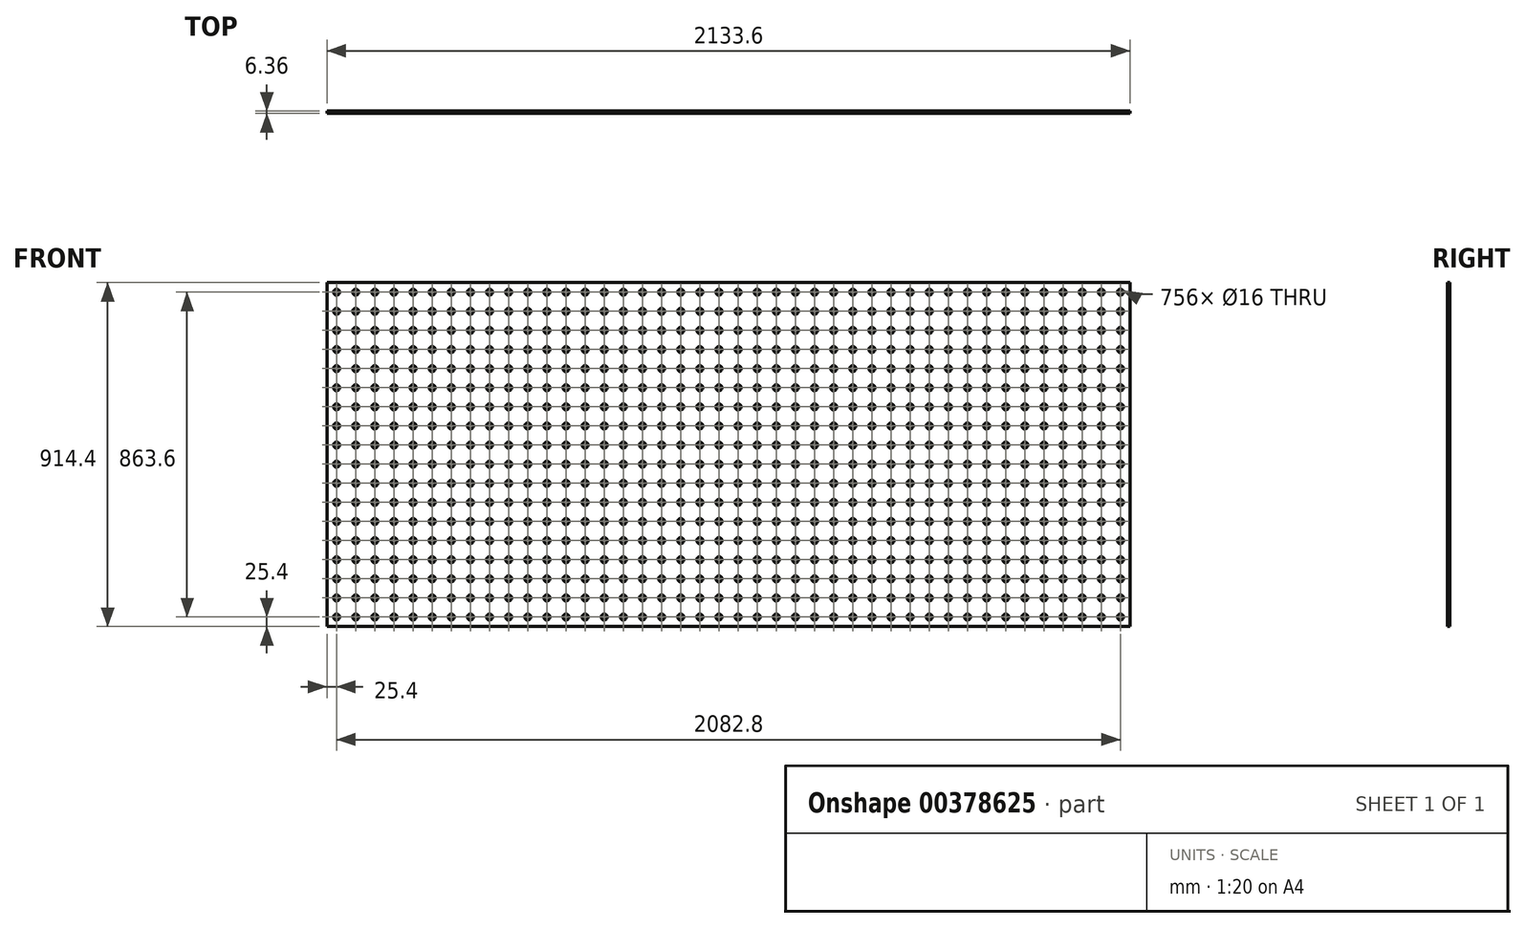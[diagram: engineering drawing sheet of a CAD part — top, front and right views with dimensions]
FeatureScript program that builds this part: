
annotation { "Feature Type Name" : "Feature", "Feature Type Description" : "" }
export const myFeature = defineFeature(function(context is Context, id is Id, definition is map)
    precondition{}
    {
        {
            var Q0;
            Q0=qCreatedBy(makeId("Front.planeOp"),FACE);
            var sketch = newSketch(context, id + "F0", { "sketchPlane" : qUnion([Q0])});
            skLineSegment(sketch, "E0.bottom", {"start": v(1066.8, 457.2) * mm, "end": v(-1066.8, 457.2) * mm});
            skLineSegment(sketch, "E0.top", {"start": v(1066.8, -457.2) * mm, "end": v(-1066.8, -457.2) * mm});
            skLineSegment(sketch, "E0.left", {"start": v(1066.8, 457.2) * mm, "end": v(1066.8, -457.2) * mm});
            skLineSegment(sketch, "E0.right", {"start": v(-1066.8, 457.2) * mm, "end": v(-1066.8, -457.2) * mm});
            skPoint(sketch, "E0.middle", {"position": v(0, 0) * mm});
            skSolve(sketch);
        }
        {
            var Q0;
            Q0 = qSketchRegion(id + "F0", true);
            extrude(context, id + "F1", {"entities" : qUnion([Q0]), "endBound" : BoundingType.SYMMETRIC, "depth" : 6.35 * mm});
        }
        {
            var Q0;
            Q0=makeQuery(id+"F1.opExtrude","CAP_FACE",FACE,{"disambiguationData":[OSD([sQuery(id+"F0.wireOp",EDGE,"E0.bottom"),sQuery(id+"F0.wireOp",EDGE,"E0.top"),sQuery(id+"F0.wireOp",EDGE,"E0.left"),sQuery(id+"F0.wireOp",EDGE,"E0.right")])],"isStart":false});
            var sketch = newSketch(context, id + "F2", { "sketchPlane" : qUnion([Q0])});
            skCircle(sketch, "E1", {"center": v(-1041.4, -431.8) * mm, "radius": 8 * mm});
            skCircle(sketch, "E2.0.1.0", {"center": v(-1041.4, -381) * mm, "radius": 8 * mm});
            skCircle(sketch, "E2.0.2.0", {"center": v(-1041.4, -330.2) * mm, "radius": 8 * mm});
            skCircle(sketch, "E2.0.3.0", {"center": v(-1041.4, -279.4) * mm, "radius": 8 * mm});
            skCircle(sketch, "E2.0.4.0", {"center": v(-1041.4, -228.6) * mm, "radius": 8 * mm});
            skCircle(sketch, "E2.0.5.0", {"center": v(-1041.4, -177.8) * mm, "radius": 8 * mm});
            skCircle(sketch, "E2.0.6.0", {"center": v(-1041.4, -127) * mm, "radius": 8 * mm});
            skCircle(sketch, "E2.0.7.0", {"center": v(-1041.4, -76.2) * mm, "radius": 8 * mm});
            skCircle(sketch, "E2.0.8.0", {"center": v(-1041.4, -25.4) * mm, "radius": 8 * mm});
            skCircle(sketch, "E2.0.9.0", {"center": v(-1041.4, 25.4) * mm, "radius": 8 * mm});
            skCircle(sketch, "E2.0.10.0", {"center": v(-1041.4, 76.2) * mm, "radius": 8 * mm});
            skCircle(sketch, "E2.0.11.0", {"center": v(-1041.4, 127) * mm, "radius": 8 * mm});
            skCircle(sketch, "E2.0.12.0", {"center": v(-1041.4, 177.8) * mm, "radius": 8 * mm});
            skCircle(sketch, "E2.0.13.0", {"center": v(-1041.4, 228.6) * mm, "radius": 8 * mm});
            skCircle(sketch, "E2.0.14.0", {"center": v(-1041.4, 279.4) * mm, "radius": 8 * mm});
            skCircle(sketch, "E2.0.15.0", {"center": v(-1041.4, 330.2) * mm, "radius": 8 * mm});
            skCircle(sketch, "E2.0.16.0", {"center": v(-1041.4, 381) * mm, "radius": 8 * mm});
            skCircle(sketch, "E2.0.17.0", {"center": v(-1041.4, 431.8) * mm, "radius": 8 * mm});
            skCircle(sketch, "E2.1.0.0", {"center": v(-990.6, -431.8) * mm, "radius": 8 * mm});
            skCircle(sketch, "E2.1.1.0", {"center": v(-990.6, -381) * mm, "radius": 8 * mm});
            skCircle(sketch, "E2.1.2.0", {"center": v(-990.6, -330.2) * mm, "radius": 8 * mm});
            skCircle(sketch, "E2.1.3.0", {"center": v(-990.6, -279.4) * mm, "radius": 8 * mm});
            skCircle(sketch, "E2.1.4.0", {"center": v(-990.6, -228.6) * mm, "radius": 8 * mm});
            skCircle(sketch, "E2.1.5.0", {"center": v(-990.6, -177.8) * mm, "radius": 8 * mm});
            skCircle(sketch, "E2.1.6.0", {"center": v(-990.6, -127) * mm, "radius": 8 * mm});
            skCircle(sketch, "E2.1.7.0", {"center": v(-990.6, -76.2) * mm, "radius": 8 * mm});
            skCircle(sketch, "E2.1.8.0", {"center": v(-990.6, -25.4) * mm, "radius": 8 * mm});
            skCircle(sketch, "E2.1.9.0", {"center": v(-990.6, 25.4) * mm, "radius": 8 * mm});
            skCircle(sketch, "E2.1.10.0", {"center": v(-990.6, 76.2) * mm, "radius": 8 * mm});
            skCircle(sketch, "E2.1.11.0", {"center": v(-990.6, 127) * mm, "radius": 8 * mm});
            skCircle(sketch, "E2.1.12.0", {"center": v(-990.6, 177.8) * mm, "radius": 8 * mm});
            skCircle(sketch, "E2.1.13.0", {"center": v(-990.6, 228.6) * mm, "radius": 8 * mm});
            skCircle(sketch, "E2.1.14.0", {"center": v(-990.6, 279.4) * mm, "radius": 8 * mm});
            skCircle(sketch, "E2.1.15.0", {"center": v(-990.6, 330.2) * mm, "radius": 8 * mm});
            skCircle(sketch, "E2.1.16.0", {"center": v(-990.6, 381) * mm, "radius": 8 * mm});
            skCircle(sketch, "E2.1.17.0", {"center": v(-990.6, 431.8) * mm, "radius": 8 * mm});
            skCircle(sketch, "E2.2.0.0", {"center": v(-939.8, -431.8) * mm, "radius": 8 * mm});
            skCircle(sketch, "E2.2.1.0", {"center": v(-939.8, -381) * mm, "radius": 8 * mm});
            skCircle(sketch, "E2.2.2.0", {"center": v(-939.8, -330.2) * mm, "radius": 8 * mm});
            skCircle(sketch, "E2.2.3.0", {"center": v(-939.8, -279.4) * mm, "radius": 8 * mm});
            skCircle(sketch, "E2.2.4.0", {"center": v(-939.8, -228.6) * mm, "radius": 8 * mm});
            skCircle(sketch, "E2.2.5.0", {"center": v(-939.8, -177.8) * mm, "radius": 8 * mm});
            skCircle(sketch, "E2.2.6.0", {"center": v(-939.8, -127) * mm, "radius": 8 * mm});
            skCircle(sketch, "E2.2.7.0", {"center": v(-939.8, -76.2) * mm, "radius": 8 * mm});
            skCircle(sketch, "E2.2.8.0", {"center": v(-939.8, -25.4) * mm, "radius": 8 * mm});
            skCircle(sketch, "E2.2.9.0", {"center": v(-939.8, 25.4) * mm, "radius": 8 * mm});
            skCircle(sketch, "E2.2.10.0", {"center": v(-939.8, 76.2) * mm, "radius": 8 * mm});
            skCircle(sketch, "E2.2.11.0", {"center": v(-939.8, 127) * mm, "radius": 8 * mm});
            skCircle(sketch, "E2.2.12.0", {"center": v(-939.8, 177.8) * mm, "radius": 8 * mm});
            skCircle(sketch, "E2.2.13.0", {"center": v(-939.8, 228.6) * mm, "radius": 8 * mm});
            skCircle(sketch, "E2.2.14.0", {"center": v(-939.8, 279.4) * mm, "radius": 8 * mm});
            skCircle(sketch, "E2.2.15.0", {"center": v(-939.8, 330.2) * mm, "radius": 8 * mm});
            skCircle(sketch, "E2.2.16.0", {"center": v(-939.8, 381) * mm, "radius": 8 * mm});
            skCircle(sketch, "E2.2.17.0", {"center": v(-939.8, 431.8) * mm, "radius": 8 * mm});
            skCircle(sketch, "E2.3.0.0", {"center": v(-889, -431.8) * mm, "radius": 8 * mm});
            skCircle(sketch, "E2.3.1.0", {"center": v(-889, -381) * mm, "radius": 8 * mm});
            skCircle(sketch, "E2.3.2.0", {"center": v(-889, -330.2) * mm, "radius": 8 * mm});
            skCircle(sketch, "E2.3.3.0", {"center": v(-889, -279.4) * mm, "radius": 8 * mm});
            skCircle(sketch, "E2.3.4.0", {"center": v(-889, -228.6) * mm, "radius": 8 * mm});
            skCircle(sketch, "E2.3.5.0", {"center": v(-889, -177.8) * mm, "radius": 8 * mm});
            skCircle(sketch, "E2.3.6.0", {"center": v(-889, -127) * mm, "radius": 8 * mm});
            skCircle(sketch, "E2.3.7.0", {"center": v(-889, -76.2) * mm, "radius": 8 * mm});
            skCircle(sketch, "E2.3.8.0", {"center": v(-889, -25.4) * mm, "radius": 8 * mm});
            skCircle(sketch, "E2.3.9.0", {"center": v(-889, 25.4) * mm, "radius": 8 * mm});
            skCircle(sketch, "E2.3.10.0", {"center": v(-889, 76.2) * mm, "radius": 8 * mm});
            skCircle(sketch, "E2.3.11.0", {"center": v(-889, 127) * mm, "radius": 8 * mm});
            skCircle(sketch, "E2.3.12.0", {"center": v(-889, 177.8) * mm, "radius": 8 * mm});
            skCircle(sketch, "E2.3.13.0", {"center": v(-889, 228.6) * mm, "radius": 8 * mm});
            skCircle(sketch, "E2.3.14.0", {"center": v(-889, 279.4) * mm, "radius": 8 * mm});
            skCircle(sketch, "E2.3.15.0", {"center": v(-889, 330.2) * mm, "radius": 8 * mm});
            skCircle(sketch, "E2.3.16.0", {"center": v(-889, 381) * mm, "radius": 8 * mm});
            skCircle(sketch, "E2.3.17.0", {"center": v(-889, 431.8) * mm, "radius": 8 * mm});
            skCircle(sketch, "E2.4.0.0", {"center": v(-838.2, -431.8) * mm, "radius": 8 * mm});
            skCircle(sketch, "E2.4.1.0", {"center": v(-838.2, -381) * mm, "radius": 8 * mm});
            skCircle(sketch, "E2.4.2.0", {"center": v(-838.2, -330.2) * mm, "radius": 8 * mm});
            skCircle(sketch, "E2.4.3.0", {"center": v(-838.2, -279.4) * mm, "radius": 8 * mm});
            skCircle(sketch, "E2.4.4.0", {"center": v(-838.2, -228.6) * mm, "radius": 8 * mm});
            skCircle(sketch, "E2.4.5.0", {"center": v(-838.2, -177.8) * mm, "radius": 8 * mm});
            skCircle(sketch, "E2.4.6.0", {"center": v(-838.2, -127) * mm, "radius": 8 * mm});
            skCircle(sketch, "E2.4.7.0", {"center": v(-838.2, -76.2) * mm, "radius": 8 * mm});
            skCircle(sketch, "E2.4.8.0", {"center": v(-838.2, -25.4) * mm, "radius": 8 * mm});
            skCircle(sketch, "E2.4.9.0", {"center": v(-838.2, 25.4) * mm, "radius": 8 * mm});
            skCircle(sketch, "E2.4.10.0", {"center": v(-838.2, 76.2) * mm, "radius": 8 * mm});
            skCircle(sketch, "E2.4.11.0", {"center": v(-838.2, 127) * mm, "radius": 8 * mm});
            skCircle(sketch, "E2.4.12.0", {"center": v(-838.2, 177.8) * mm, "radius": 8 * mm});
            skCircle(sketch, "E2.4.13.0", {"center": v(-838.2, 228.6) * mm, "radius": 8 * mm});
            skCircle(sketch, "E2.4.14.0", {"center": v(-838.2, 279.4) * mm, "radius": 8 * mm});
            skCircle(sketch, "E2.4.15.0", {"center": v(-838.2, 330.2) * mm, "radius": 8 * mm});
            skCircle(sketch, "E2.4.16.0", {"center": v(-838.2, 381) * mm, "radius": 8 * mm});
            skCircle(sketch, "E2.4.17.0", {"center": v(-838.2, 431.8) * mm, "radius": 8 * mm});
            skCircle(sketch, "E2.5.0.0", {"center": v(-787.4, -431.8) * mm, "radius": 8 * mm});
            skCircle(sketch, "E2.5.1.0", {"center": v(-787.4, -381) * mm, "radius": 8 * mm});
            skCircle(sketch, "E2.5.2.0", {"center": v(-787.4, -330.2) * mm, "radius": 8 * mm});
            skCircle(sketch, "E2.5.3.0", {"center": v(-787.4, -279.4) * mm, "radius": 8 * mm});
            skCircle(sketch, "E2.5.4.0", {"center": v(-787.4, -228.6) * mm, "radius": 8 * mm});
            skCircle(sketch, "E2.5.5.0", {"center": v(-787.4, -177.8) * mm, "radius": 8 * mm});
            skCircle(sketch, "E2.5.6.0", {"center": v(-787.4, -127) * mm, "radius": 8 * mm});
            skCircle(sketch, "E2.5.7.0", {"center": v(-787.4, -76.2) * mm, "radius": 8 * mm});
            skCircle(sketch, "E2.5.8.0", {"center": v(-787.4, -25.4) * mm, "radius": 8 * mm});
            skCircle(sketch, "E2.5.9.0", {"center": v(-787.4, 25.4) * mm, "radius": 8 * mm});
            skCircle(sketch, "E2.5.10.0", {"center": v(-787.4, 76.2) * mm, "radius": 8 * mm});
            skCircle(sketch, "E2.5.11.0", {"center": v(-787.4, 127) * mm, "radius": 8 * mm});
            skCircle(sketch, "E2.5.12.0", {"center": v(-787.4, 177.8) * mm, "radius": 8 * mm});
            skCircle(sketch, "E2.5.13.0", {"center": v(-787.4, 228.6) * mm, "radius": 8 * mm});
            skCircle(sketch, "E2.5.14.0", {"center": v(-787.4, 279.4) * mm, "radius": 8 * mm});
            skCircle(sketch, "E2.5.15.0", {"center": v(-787.4, 330.2) * mm, "radius": 8 * mm});
            skCircle(sketch, "E2.5.16.0", {"center": v(-787.4, 381) * mm, "radius": 8 * mm});
            skCircle(sketch, "E2.5.17.0", {"center": v(-787.4, 431.8) * mm, "radius": 8 * mm});
            skCircle(sketch, "E2.6.0.0", {"center": v(-736.6, -431.8) * mm, "radius": 8 * mm});
            skCircle(sketch, "E2.6.1.0", {"center": v(-736.6, -381) * mm, "radius": 8 * mm});
            skCircle(sketch, "E2.6.2.0", {"center": v(-736.6, -330.2) * mm, "radius": 8 * mm});
            skCircle(sketch, "E2.6.3.0", {"center": v(-736.6, -279.4) * mm, "radius": 8 * mm});
            skCircle(sketch, "E2.6.4.0", {"center": v(-736.6, -228.6) * mm, "radius": 8 * mm});
            skCircle(sketch, "E2.6.5.0", {"center": v(-736.6, -177.8) * mm, "radius": 8 * mm});
            skCircle(sketch, "E2.6.6.0", {"center": v(-736.6, -127) * mm, "radius": 8 * mm});
            skCircle(sketch, "E2.6.7.0", {"center": v(-736.6, -76.2) * mm, "radius": 8 * mm});
            skCircle(sketch, "E2.6.8.0", {"center": v(-736.6, -25.4) * mm, "radius": 8 * mm});
            skCircle(sketch, "E2.6.9.0", {"center": v(-736.6, 25.4) * mm, "radius": 8 * mm});
            skCircle(sketch, "E2.6.10.0", {"center": v(-736.6, 76.2) * mm, "radius": 8 * mm});
            skCircle(sketch, "E2.6.11.0", {"center": v(-736.6, 127) * mm, "radius": 8 * mm});
            skCircle(sketch, "E2.6.12.0", {"center": v(-736.6, 177.8) * mm, "radius": 8 * mm});
            skCircle(sketch, "E2.6.13.0", {"center": v(-736.6, 228.6) * mm, "radius": 8 * mm});
            skCircle(sketch, "E2.6.14.0", {"center": v(-736.6, 279.4) * mm, "radius": 8 * mm});
            skCircle(sketch, "E2.6.15.0", {"center": v(-736.6, 330.2) * mm, "radius": 8 * mm});
            skCircle(sketch, "E2.6.16.0", {"center": v(-736.6, 381) * mm, "radius": 8 * mm});
            skCircle(sketch, "E2.6.17.0", {"center": v(-736.6, 431.8) * mm, "radius": 8 * mm});
            skCircle(sketch, "E2.7.0.0", {"center": v(-685.8, -431.8) * mm, "radius": 8 * mm});
            skCircle(sketch, "E2.7.1.0", {"center": v(-685.8, -381) * mm, "radius": 8 * mm});
            skCircle(sketch, "E2.7.2.0", {"center": v(-685.8, -330.2) * mm, "radius": 8 * mm});
            skCircle(sketch, "E2.7.3.0", {"center": v(-685.8, -279.4) * mm, "radius": 8 * mm});
            skCircle(sketch, "E2.7.4.0", {"center": v(-685.8, -228.6) * mm, "radius": 8 * mm});
            skCircle(sketch, "E2.7.5.0", {"center": v(-685.8, -177.8) * mm, "radius": 8 * mm});
            skCircle(sketch, "E2.7.6.0", {"center": v(-685.8, -127) * mm, "radius": 8 * mm});
            skCircle(sketch, "E2.7.7.0", {"center": v(-685.8, -76.2) * mm, "radius": 8 * mm});
            skCircle(sketch, "E2.7.8.0", {"center": v(-685.8, -25.4) * mm, "radius": 8 * mm});
            skCircle(sketch, "E2.7.9.0", {"center": v(-685.8, 25.4) * mm, "radius": 8 * mm});
            skCircle(sketch, "E2.7.10.0", {"center": v(-685.8, 76.2) * mm, "radius": 8 * mm});
            skCircle(sketch, "E2.7.11.0", {"center": v(-685.8, 127) * mm, "radius": 8 * mm});
            skCircle(sketch, "E2.7.12.0", {"center": v(-685.8, 177.8) * mm, "radius": 8 * mm});
            skCircle(sketch, "E2.7.13.0", {"center": v(-685.8, 228.6) * mm, "radius": 8 * mm});
            skCircle(sketch, "E2.7.14.0", {"center": v(-685.8, 279.4) * mm, "radius": 8 * mm});
            skCircle(sketch, "E2.7.15.0", {"center": v(-685.8, 330.2) * mm, "radius": 8 * mm});
            skCircle(sketch, "E2.7.16.0", {"center": v(-685.8, 381) * mm, "radius": 8 * mm});
            skCircle(sketch, "E2.7.17.0", {"center": v(-685.8, 431.8) * mm, "radius": 8 * mm});
            skCircle(sketch, "E2.8.0.0", {"center": v(-635, -431.8) * mm, "radius": 8 * mm});
            skCircle(sketch, "E2.8.1.0", {"center": v(-635, -381) * mm, "radius": 8 * mm});
            skCircle(sketch, "E2.8.2.0", {"center": v(-635, -330.2) * mm, "radius": 8 * mm});
            skCircle(sketch, "E2.8.3.0", {"center": v(-635, -279.4) * mm, "radius": 8 * mm});
            skCircle(sketch, "E2.8.4.0", {"center": v(-635, -228.6) * mm, "radius": 8 * mm});
            skCircle(sketch, "E2.8.5.0", {"center": v(-635, -177.8) * mm, "radius": 8 * mm});
            skCircle(sketch, "E2.8.6.0", {"center": v(-635, -127) * mm, "radius": 8 * mm});
            skCircle(sketch, "E2.8.7.0", {"center": v(-635, -76.2) * mm, "radius": 8 * mm});
            skCircle(sketch, "E2.8.8.0", {"center": v(-635, -25.4) * mm, "radius": 8 * mm});
            skCircle(sketch, "E2.8.9.0", {"center": v(-635, 25.4) * mm, "radius": 8 * mm});
            skCircle(sketch, "E2.8.10.0", {"center": v(-635, 76.2) * mm, "radius": 8 * mm});
            skCircle(sketch, "E2.8.11.0", {"center": v(-635, 127) * mm, "radius": 8 * mm});
            skCircle(sketch, "E2.8.12.0", {"center": v(-635, 177.8) * mm, "radius": 8 * mm});
            skCircle(sketch, "E2.8.13.0", {"center": v(-635, 228.6) * mm, "radius": 8 * mm});
            skCircle(sketch, "E2.8.14.0", {"center": v(-635, 279.4) * mm, "radius": 8 * mm});
            skCircle(sketch, "E2.8.15.0", {"center": v(-635, 330.2) * mm, "radius": 8 * mm});
            skCircle(sketch, "E2.8.16.0", {"center": v(-635, 381) * mm, "radius": 8 * mm});
            skCircle(sketch, "E2.8.17.0", {"center": v(-635, 431.8) * mm, "radius": 8 * mm});
            skCircle(sketch, "E2.9.0.0", {"center": v(-584.2, -431.8) * mm, "radius": 8 * mm});
            skCircle(sketch, "E2.9.1.0", {"center": v(-584.2, -381) * mm, "radius": 8 * mm});
            skCircle(sketch, "E2.9.2.0", {"center": v(-584.2, -330.2) * mm, "radius": 8 * mm});
            skCircle(sketch, "E2.9.3.0", {"center": v(-584.2, -279.4) * mm, "radius": 8 * mm});
            skCircle(sketch, "E2.9.4.0", {"center": v(-584.2, -228.6) * mm, "radius": 8 * mm});
            skCircle(sketch, "E2.9.5.0", {"center": v(-584.2, -177.8) * mm, "radius": 8 * mm});
            skCircle(sketch, "E2.9.6.0", {"center": v(-584.2, -127) * mm, "radius": 8 * mm});
            skCircle(sketch, "E2.9.7.0", {"center": v(-584.2, -76.2) * mm, "radius": 8 * mm});
            skCircle(sketch, "E2.9.8.0", {"center": v(-584.2, -25.4) * mm, "radius": 8 * mm});
            skCircle(sketch, "E2.9.9.0", {"center": v(-584.2, 25.4) * mm, "radius": 8 * mm});
            skCircle(sketch, "E2.9.10.0", {"center": v(-584.2, 76.2) * mm, "radius": 8 * mm});
            skCircle(sketch, "E2.9.11.0", {"center": v(-584.2, 127) * mm, "radius": 8 * mm});
            skCircle(sketch, "E2.9.12.0", {"center": v(-584.2, 177.8) * mm, "radius": 8 * mm});
            skCircle(sketch, "E2.9.13.0", {"center": v(-584.2, 228.6) * mm, "radius": 8 * mm});
            skCircle(sketch, "E2.9.14.0", {"center": v(-584.2, 279.4) * mm, "radius": 8 * mm});
            skCircle(sketch, "E2.9.15.0", {"center": v(-584.2, 330.2) * mm, "radius": 8 * mm});
            skCircle(sketch, "E2.9.16.0", {"center": v(-584.2, 381) * mm, "radius": 8 * mm});
            skCircle(sketch, "E2.9.17.0", {"center": v(-584.2, 431.8) * mm, "radius": 8 * mm});
            skCircle(sketch, "E2.10.0.0", {"center": v(-533.4, -431.8) * mm, "radius": 8 * mm});
            skCircle(sketch, "E2.10.1.0", {"center": v(-533.4, -381) * mm, "radius": 8 * mm});
            skCircle(sketch, "E2.10.2.0", {"center": v(-533.4, -330.2) * mm, "radius": 8 * mm});
            skCircle(sketch, "E2.10.3.0", {"center": v(-533.4, -279.4) * mm, "radius": 8 * mm});
            skCircle(sketch, "E2.10.4.0", {"center": v(-533.4, -228.6) * mm, "radius": 8 * mm});
            skCircle(sketch, "E2.10.5.0", {"center": v(-533.4, -177.8) * mm, "radius": 8 * mm});
            skCircle(sketch, "E2.10.6.0", {"center": v(-533.4, -127) * mm, "radius": 8 * mm});
            skCircle(sketch, "E2.10.7.0", {"center": v(-533.4, -76.2) * mm, "radius": 8 * mm});
            skCircle(sketch, "E2.10.8.0", {"center": v(-533.4, -25.4) * mm, "radius": 8 * mm});
            skCircle(sketch, "E2.10.9.0", {"center": v(-533.4, 25.4) * mm, "radius": 8 * mm});
            skCircle(sketch, "E2.10.10.0", {"center": v(-533.4, 76.2) * mm, "radius": 8 * mm});
            skCircle(sketch, "E2.10.11.0", {"center": v(-533.4, 127) * mm, "radius": 8 * mm});
            skCircle(sketch, "E2.10.12.0", {"center": v(-533.4, 177.8) * mm, "radius": 8 * mm});
            skCircle(sketch, "E2.10.13.0", {"center": v(-533.4, 228.6) * mm, "radius": 8 * mm});
            skCircle(sketch, "E2.10.14.0", {"center": v(-533.4, 279.4) * mm, "radius": 8 * mm});
            skCircle(sketch, "E2.10.15.0", {"center": v(-533.4, 330.2) * mm, "radius": 8 * mm});
            skCircle(sketch, "E2.10.16.0", {"center": v(-533.4, 381) * mm, "radius": 8 * mm});
            skCircle(sketch, "E2.10.17.0", {"center": v(-533.4, 431.8) * mm, "radius": 8 * mm});
            skCircle(sketch, "E2.11.0.0", {"center": v(-482.6, -431.8) * mm, "radius": 8 * mm});
            skCircle(sketch, "E2.11.1.0", {"center": v(-482.6, -381) * mm, "radius": 8 * mm});
            skCircle(sketch, "E2.11.2.0", {"center": v(-482.6, -330.2) * mm, "radius": 8 * mm});
            skCircle(sketch, "E2.11.3.0", {"center": v(-482.6, -279.4) * mm, "radius": 8 * mm});
            skCircle(sketch, "E2.11.4.0", {"center": v(-482.6, -228.6) * mm, "radius": 8 * mm});
            skCircle(sketch, "E2.11.5.0", {"center": v(-482.6, -177.8) * mm, "radius": 8 * mm});
            skCircle(sketch, "E2.11.6.0", {"center": v(-482.6, -127) * mm, "radius": 8 * mm});
            skCircle(sketch, "E2.11.7.0", {"center": v(-482.6, -76.2) * mm, "radius": 8 * mm});
            skCircle(sketch, "E2.11.8.0", {"center": v(-482.6, -25.4) * mm, "radius": 8 * mm});
            skCircle(sketch, "E2.11.9.0", {"center": v(-482.6, 25.4) * mm, "radius": 8 * mm});
            skCircle(sketch, "E2.11.10.0", {"center": v(-482.6, 76.2) * mm, "radius": 8 * mm});
            skCircle(sketch, "E2.11.11.0", {"center": v(-482.6, 127) * mm, "radius": 8 * mm});
            skCircle(sketch, "E2.11.12.0", {"center": v(-482.6, 177.8) * mm, "radius": 8 * mm});
            skCircle(sketch, "E2.11.13.0", {"center": v(-482.6, 228.6) * mm, "radius": 8 * mm});
            skCircle(sketch, "E2.11.14.0", {"center": v(-482.6, 279.4) * mm, "radius": 8 * mm});
            skCircle(sketch, "E2.11.15.0", {"center": v(-482.6, 330.2) * mm, "radius": 8 * mm});
            skCircle(sketch, "E2.11.16.0", {"center": v(-482.6, 381) * mm, "radius": 8 * mm});
            skCircle(sketch, "E2.11.17.0", {"center": v(-482.6, 431.8) * mm, "radius": 8 * mm});
            skCircle(sketch, "E2.12.0.0", {"center": v(-431.8, -431.8) * mm, "radius": 8 * mm});
            skCircle(sketch, "E2.12.1.0", {"center": v(-431.8, -381) * mm, "radius": 8 * mm});
            skCircle(sketch, "E2.12.2.0", {"center": v(-431.8, -330.2) * mm, "radius": 8 * mm});
            skCircle(sketch, "E2.12.3.0", {"center": v(-431.8, -279.4) * mm, "radius": 8 * mm});
            skCircle(sketch, "E2.12.4.0", {"center": v(-431.8, -228.6) * mm, "radius": 8 * mm});
            skCircle(sketch, "E2.12.5.0", {"center": v(-431.8, -177.8) * mm, "radius": 8 * mm});
            skCircle(sketch, "E2.12.6.0", {"center": v(-431.8, -127) * mm, "radius": 8 * mm});
            skCircle(sketch, "E2.12.7.0", {"center": v(-431.8, -76.2) * mm, "radius": 8 * mm});
            skCircle(sketch, "E2.12.8.0", {"center": v(-431.8, -25.4) * mm, "radius": 8 * mm});
            skCircle(sketch, "E2.12.9.0", {"center": v(-431.8, 25.4) * mm, "radius": 8 * mm});
            skCircle(sketch, "E2.12.10.0", {"center": v(-431.8, 76.2) * mm, "radius": 8 * mm});
            skCircle(sketch, "E2.12.11.0", {"center": v(-431.8, 127) * mm, "radius": 8 * mm});
            skCircle(sketch, "E2.12.12.0", {"center": v(-431.8, 177.8) * mm, "radius": 8 * mm});
            skCircle(sketch, "E2.12.13.0", {"center": v(-431.8, 228.6) * mm, "radius": 8 * mm});
            skCircle(sketch, "E2.12.14.0", {"center": v(-431.8, 279.4) * mm, "radius": 8 * mm});
            skCircle(sketch, "E2.12.15.0", {"center": v(-431.8, 330.2) * mm, "radius": 8 * mm});
            skCircle(sketch, "E2.12.16.0", {"center": v(-431.8, 381) * mm, "radius": 8 * mm});
            skCircle(sketch, "E2.12.17.0", {"center": v(-431.8, 431.8) * mm, "radius": 8 * mm});
            skCircle(sketch, "E2.13.0.0", {"center": v(-381, -431.8) * mm, "radius": 8 * mm});
            skCircle(sketch, "E2.13.1.0", {"center": v(-381, -381) * mm, "radius": 8 * mm});
            skCircle(sketch, "E2.13.2.0", {"center": v(-381, -330.2) * mm, "radius": 8 * mm});
            skCircle(sketch, "E2.13.3.0", {"center": v(-381, -279.4) * mm, "radius": 8 * mm});
            skCircle(sketch, "E2.13.4.0", {"center": v(-381, -228.6) * mm, "radius": 8 * mm});
            skCircle(sketch, "E2.13.5.0", {"center": v(-381, -177.8) * mm, "radius": 8 * mm});
            skCircle(sketch, "E2.13.6.0", {"center": v(-381, -127) * mm, "radius": 8 * mm});
            skCircle(sketch, "E2.13.7.0", {"center": v(-381, -76.2) * mm, "radius": 8 * mm});
            skCircle(sketch, "E2.13.8.0", {"center": v(-381, -25.4) * mm, "radius": 8 * mm});
            skCircle(sketch, "E2.13.9.0", {"center": v(-381, 25.4) * mm, "radius": 8 * mm});
            skCircle(sketch, "E2.13.10.0", {"center": v(-381, 76.2) * mm, "radius": 8 * mm});
            skCircle(sketch, "E2.13.11.0", {"center": v(-381, 127) * mm, "radius": 8 * mm});
            skCircle(sketch, "E2.13.12.0", {"center": v(-381, 177.8) * mm, "radius": 8 * mm});
            skCircle(sketch, "E2.13.13.0", {"center": v(-381, 228.6) * mm, "radius": 8 * mm});
            skCircle(sketch, "E2.13.14.0", {"center": v(-381, 279.4) * mm, "radius": 8 * mm});
            skCircle(sketch, "E2.13.15.0", {"center": v(-381, 330.2) * mm, "radius": 8 * mm});
            skCircle(sketch, "E2.13.16.0", {"center": v(-381, 381) * mm, "radius": 8 * mm});
            skCircle(sketch, "E2.13.17.0", {"center": v(-381, 431.8) * mm, "radius": 8 * mm});
            skCircle(sketch, "E2.14.0.0", {"center": v(-330.2, -431.8) * mm, "radius": 8 * mm});
            skCircle(sketch, "E2.14.1.0", {"center": v(-330.2, -381) * mm, "radius": 8 * mm});
            skCircle(sketch, "E2.14.2.0", {"center": v(-330.2, -330.2) * mm, "radius": 8 * mm});
            skCircle(sketch, "E2.14.3.0", {"center": v(-330.2, -279.4) * mm, "radius": 8 * mm});
            skCircle(sketch, "E2.14.4.0", {"center": v(-330.2, -228.6) * mm, "radius": 8 * mm});
            skCircle(sketch, "E2.14.5.0", {"center": v(-330.2, -177.8) * mm, "radius": 8 * mm});
            skCircle(sketch, "E2.14.6.0", {"center": v(-330.2, -127) * mm, "radius": 8 * mm});
            skCircle(sketch, "E2.14.7.0", {"center": v(-330.2, -76.2) * mm, "radius": 8 * mm});
            skCircle(sketch, "E2.14.8.0", {"center": v(-330.2, -25.4) * mm, "radius": 8 * mm});
            skCircle(sketch, "E2.14.9.0", {"center": v(-330.2, 25.4) * mm, "radius": 8 * mm});
            skCircle(sketch, "E2.14.10.0", {"center": v(-330.2, 76.2) * mm, "radius": 8 * mm});
            skCircle(sketch, "E2.14.11.0", {"center": v(-330.2, 127) * mm, "radius": 8 * mm});
            skCircle(sketch, "E2.14.12.0", {"center": v(-330.2, 177.8) * mm, "radius": 8 * mm});
            skCircle(sketch, "E2.14.13.0", {"center": v(-330.2, 228.6) * mm, "radius": 8 * mm});
            skCircle(sketch, "E2.14.14.0", {"center": v(-330.2, 279.4) * mm, "radius": 8 * mm});
            skCircle(sketch, "E2.14.15.0", {"center": v(-330.2, 330.2) * mm, "radius": 8 * mm});
            skCircle(sketch, "E2.14.16.0", {"center": v(-330.2, 381) * mm, "radius": 8 * mm});
            skCircle(sketch, "E2.14.17.0", {"center": v(-330.2, 431.8) * mm, "radius": 8 * mm});
            skCircle(sketch, "E2.15.0.0", {"center": v(-279.4, -431.8) * mm, "radius": 8 * mm});
            skCircle(sketch, "E2.15.1.0", {"center": v(-279.4, -381) * mm, "radius": 8 * mm});
            skCircle(sketch, "E2.15.2.0", {"center": v(-279.4, -330.2) * mm, "radius": 8 * mm});
            skCircle(sketch, "E2.15.3.0", {"center": v(-279.4, -279.4) * mm, "radius": 8 * mm});
            skCircle(sketch, "E2.15.4.0", {"center": v(-279.4, -228.6) * mm, "radius": 8 * mm});
            skCircle(sketch, "E2.15.5.0", {"center": v(-279.4, -177.8) * mm, "radius": 8 * mm});
            skCircle(sketch, "E2.15.6.0", {"center": v(-279.4, -127) * mm, "radius": 8 * mm});
            skCircle(sketch, "E2.15.7.0", {"center": v(-279.4, -76.2) * mm, "radius": 8 * mm});
            skCircle(sketch, "E2.15.8.0", {"center": v(-279.4, -25.4) * mm, "radius": 8 * mm});
            skCircle(sketch, "E2.15.9.0", {"center": v(-279.4, 25.4) * mm, "radius": 8 * mm});
            skCircle(sketch, "E2.15.10.0", {"center": v(-279.4, 76.2) * mm, "radius": 8 * mm});
            skCircle(sketch, "E2.15.11.0", {"center": v(-279.4, 127) * mm, "radius": 8 * mm});
            skCircle(sketch, "E2.15.12.0", {"center": v(-279.4, 177.8) * mm, "radius": 8 * mm});
            skCircle(sketch, "E2.15.13.0", {"center": v(-279.4, 228.6) * mm, "radius": 8 * mm});
            skCircle(sketch, "E2.15.14.0", {"center": v(-279.4, 279.4) * mm, "radius": 8 * mm});
            skCircle(sketch, "E2.15.15.0", {"center": v(-279.4, 330.2) * mm, "radius": 8 * mm});
            skCircle(sketch, "E2.15.16.0", {"center": v(-279.4, 381) * mm, "radius": 8 * mm});
            skCircle(sketch, "E2.15.17.0", {"center": v(-279.4, 431.8) * mm, "radius": 8 * mm});
            skCircle(sketch, "E2.16.0.0", {"center": v(-228.6, -431.8) * mm, "radius": 8 * mm});
            skCircle(sketch, "E2.16.1.0", {"center": v(-228.6, -381) * mm, "radius": 8 * mm});
            skCircle(sketch, "E2.16.2.0", {"center": v(-228.6, -330.2) * mm, "radius": 8 * mm});
            skCircle(sketch, "E2.16.3.0", {"center": v(-228.6, -279.4) * mm, "radius": 8 * mm});
            skCircle(sketch, "E2.16.4.0", {"center": v(-228.6, -228.6) * mm, "radius": 8 * mm});
            skCircle(sketch, "E2.16.5.0", {"center": v(-228.6, -177.8) * mm, "radius": 8 * mm});
            skCircle(sketch, "E2.16.6.0", {"center": v(-228.6, -127) * mm, "radius": 8 * mm});
            skCircle(sketch, "E2.16.7.0", {"center": v(-228.6, -76.2) * mm, "radius": 8 * mm});
            skCircle(sketch, "E2.16.8.0", {"center": v(-228.6, -25.4) * mm, "radius": 8 * mm});
            skCircle(sketch, "E2.16.9.0", {"center": v(-228.6, 25.4) * mm, "radius": 8 * mm});
            skCircle(sketch, "E2.16.10.0", {"center": v(-228.6, 76.2) * mm, "radius": 8 * mm});
            skCircle(sketch, "E2.16.11.0", {"center": v(-228.6, 127) * mm, "radius": 8 * mm});
            skCircle(sketch, "E2.16.12.0", {"center": v(-228.6, 177.8) * mm, "radius": 8 * mm});
            skCircle(sketch, "E2.16.13.0", {"center": v(-228.6, 228.6) * mm, "radius": 8 * mm});
            skCircle(sketch, "E2.16.14.0", {"center": v(-228.6, 279.4) * mm, "radius": 8 * mm});
            skCircle(sketch, "E2.16.15.0", {"center": v(-228.6, 330.2) * mm, "radius": 8 * mm});
            skCircle(sketch, "E2.16.16.0", {"center": v(-228.6, 381) * mm, "radius": 8 * mm});
            skCircle(sketch, "E2.16.17.0", {"center": v(-228.6, 431.8) * mm, "radius": 8 * mm});
            skCircle(sketch, "E2.17.0.0", {"center": v(-177.8, -431.8) * mm, "radius": 8 * mm});
            skCircle(sketch, "E2.17.1.0", {"center": v(-177.8, -381) * mm, "radius": 8 * mm});
            skCircle(sketch, "E2.17.2.0", {"center": v(-177.8, -330.2) * mm, "radius": 8 * mm});
            skCircle(sketch, "E2.17.3.0", {"center": v(-177.8, -279.4) * mm, "radius": 8 * mm});
            skCircle(sketch, "E2.17.4.0", {"center": v(-177.8, -228.6) * mm, "radius": 8 * mm});
            skCircle(sketch, "E2.17.5.0", {"center": v(-177.8, -177.8) * mm, "radius": 8 * mm});
            skCircle(sketch, "E2.17.6.0", {"center": v(-177.8, -127) * mm, "radius": 8 * mm});
            skCircle(sketch, "E2.17.7.0", {"center": v(-177.8, -76.2) * mm, "radius": 8 * mm});
            skCircle(sketch, "E2.17.8.0", {"center": v(-177.8, -25.4) * mm, "radius": 8 * mm});
            skCircle(sketch, "E2.17.9.0", {"center": v(-177.8, 25.4) * mm, "radius": 8 * mm});
            skCircle(sketch, "E2.17.10.0", {"center": v(-177.8, 76.2) * mm, "radius": 8 * mm});
            skCircle(sketch, "E2.17.11.0", {"center": v(-177.8, 127) * mm, "radius": 8 * mm});
            skCircle(sketch, "E2.17.12.0", {"center": v(-177.8, 177.8) * mm, "radius": 8 * mm});
            skCircle(sketch, "E2.17.13.0", {"center": v(-177.8, 228.6) * mm, "radius": 8 * mm});
            skCircle(sketch, "E2.17.14.0", {"center": v(-177.8, 279.4) * mm, "radius": 8 * mm});
            skCircle(sketch, "E2.17.15.0", {"center": v(-177.8, 330.2) * mm, "radius": 8 * mm});
            skCircle(sketch, "E2.17.16.0", {"center": v(-177.8, 381) * mm, "radius": 8 * mm});
            skCircle(sketch, "E2.17.17.0", {"center": v(-177.8, 431.8) * mm, "radius": 8 * mm});
            skCircle(sketch, "E2.18.0.0", {"center": v(-127, -431.8) * mm, "radius": 8 * mm});
            skCircle(sketch, "E2.18.1.0", {"center": v(-127, -381) * mm, "radius": 8 * mm});
            skCircle(sketch, "E2.18.2.0", {"center": v(-127, -330.2) * mm, "radius": 8 * mm});
            skCircle(sketch, "E2.18.3.0", {"center": v(-127, -279.4) * mm, "radius": 8 * mm});
            skCircle(sketch, "E2.18.4.0", {"center": v(-127, -228.6) * mm, "radius": 8 * mm});
            skCircle(sketch, "E2.18.5.0", {"center": v(-127, -177.8) * mm, "radius": 8 * mm});
            skCircle(sketch, "E2.18.6.0", {"center": v(-127, -127) * mm, "radius": 8 * mm});
            skCircle(sketch, "E2.18.7.0", {"center": v(-127, -76.2) * mm, "radius": 8 * mm});
            skCircle(sketch, "E2.18.8.0", {"center": v(-127, -25.4) * mm, "radius": 8 * mm});
            skCircle(sketch, "E2.18.9.0", {"center": v(-127, 25.4) * mm, "radius": 8 * mm});
            skCircle(sketch, "E2.18.10.0", {"center": v(-127, 76.2) * mm, "radius": 8 * mm});
            skCircle(sketch, "E2.18.11.0", {"center": v(-127, 127) * mm, "radius": 8 * mm});
            skCircle(sketch, "E2.18.12.0", {"center": v(-127, 177.8) * mm, "radius": 8 * mm});
            skCircle(sketch, "E2.18.13.0", {"center": v(-127, 228.6) * mm, "radius": 8 * mm});
            skCircle(sketch, "E2.18.14.0", {"center": v(-127, 279.4) * mm, "radius": 8 * mm});
            skCircle(sketch, "E2.18.15.0", {"center": v(-127, 330.2) * mm, "radius": 8 * mm});
            skCircle(sketch, "E2.18.16.0", {"center": v(-127, 381) * mm, "radius": 8 * mm});
            skCircle(sketch, "E2.18.17.0", {"center": v(-127, 431.8) * mm, "radius": 8 * mm});
            skCircle(sketch, "E2.19.0.0", {"center": v(-76.2, -431.8) * mm, "radius": 8 * mm});
            skCircle(sketch, "E2.19.1.0", {"center": v(-76.2, -381) * mm, "radius": 8 * mm});
            skCircle(sketch, "E2.19.2.0", {"center": v(-76.2, -330.2) * mm, "radius": 8 * mm});
            skCircle(sketch, "E2.19.3.0", {"center": v(-76.2, -279.4) * mm, "radius": 8 * mm});
            skCircle(sketch, "E2.19.4.0", {"center": v(-76.2, -228.6) * mm, "radius": 8 * mm});
            skCircle(sketch, "E2.19.5.0", {"center": v(-76.2, -177.8) * mm, "radius": 8 * mm});
            skCircle(sketch, "E2.19.6.0", {"center": v(-76.2, -127) * mm, "radius": 8 * mm});
            skCircle(sketch, "E2.19.7.0", {"center": v(-76.2, -76.2) * mm, "radius": 8 * mm});
            skCircle(sketch, "E2.19.8.0", {"center": v(-76.2, -25.4) * mm, "radius": 8 * mm});
            skCircle(sketch, "E2.19.9.0", {"center": v(-76.2, 25.4) * mm, "radius": 8 * mm});
            skCircle(sketch, "E2.19.10.0", {"center": v(-76.2, 76.2) * mm, "radius": 8 * mm});
            skCircle(sketch, "E2.19.11.0", {"center": v(-76.2, 127) * mm, "radius": 8 * mm});
            skCircle(sketch, "E2.19.12.0", {"center": v(-76.2, 177.8) * mm, "radius": 8 * mm});
            skCircle(sketch, "E2.19.13.0", {"center": v(-76.2, 228.6) * mm, "radius": 8 * mm});
            skCircle(sketch, "E2.19.14.0", {"center": v(-76.2, 279.4) * mm, "radius": 8 * mm});
            skCircle(sketch, "E2.19.15.0", {"center": v(-76.2, 330.2) * mm, "radius": 8 * mm});
            skCircle(sketch, "E2.19.16.0", {"center": v(-76.2, 381) * mm, "radius": 8 * mm});
            skCircle(sketch, "E2.19.17.0", {"center": v(-76.2, 431.8) * mm, "radius": 8 * mm});
            skCircle(sketch, "E2.20.0.0", {"center": v(-25.4, -431.8) * mm, "radius": 8 * mm});
            skCircle(sketch, "E2.20.1.0", {"center": v(-25.4, -381) * mm, "radius": 8 * mm});
            skCircle(sketch, "E2.20.2.0", {"center": v(-25.4, -330.2) * mm, "radius": 8 * mm});
            skCircle(sketch, "E2.20.3.0", {"center": v(-25.4, -279.4) * mm, "radius": 8 * mm});
            skCircle(sketch, "E2.20.4.0", {"center": v(-25.4, -228.6) * mm, "radius": 8 * mm});
            skCircle(sketch, "E2.20.5.0", {"center": v(-25.4, -177.8) * mm, "radius": 8 * mm});
            skCircle(sketch, "E2.20.6.0", {"center": v(-25.4, -127) * mm, "radius": 8 * mm});
            skCircle(sketch, "E2.20.7.0", {"center": v(-25.4, -76.2) * mm, "radius": 8 * mm});
            skCircle(sketch, "E2.20.8.0", {"center": v(-25.4, -25.4) * mm, "radius": 8 * mm});
            skCircle(sketch, "E2.20.9.0", {"center": v(-25.4, 25.4) * mm, "radius": 8 * mm});
            skCircle(sketch, "E2.20.10.0", {"center": v(-25.4, 76.2) * mm, "radius": 8 * mm});
            skCircle(sketch, "E2.20.11.0", {"center": v(-25.4, 127) * mm, "radius": 8 * mm});
            skCircle(sketch, "E2.20.12.0", {"center": v(-25.4, 177.8) * mm, "radius": 8 * mm});
            skCircle(sketch, "E2.20.13.0", {"center": v(-25.4, 228.6) * mm, "radius": 8 * mm});
            skCircle(sketch, "E2.20.14.0", {"center": v(-25.4, 279.4) * mm, "radius": 8 * mm});
            skCircle(sketch, "E2.20.15.0", {"center": v(-25.4, 330.2) * mm, "radius": 8 * mm});
            skCircle(sketch, "E2.20.16.0", {"center": v(-25.4, 381) * mm, "radius": 8 * mm});
            skCircle(sketch, "E2.20.17.0", {"center": v(-25.4, 431.8) * mm, "radius": 8 * mm});
            skCircle(sketch, "E2.21.0.0", {"center": v(25.4, -431.8) * mm, "radius": 8 * mm});
            skCircle(sketch, "E2.21.1.0", {"center": v(25.4, -381) * mm, "radius": 8 * mm});
            skCircle(sketch, "E2.21.2.0", {"center": v(25.4, -330.2) * mm, "radius": 8 * mm});
            skCircle(sketch, "E2.21.3.0", {"center": v(25.4, -279.4) * mm, "radius": 8 * mm});
            skCircle(sketch, "E2.21.4.0", {"center": v(25.4, -228.6) * mm, "radius": 8 * mm});
            skCircle(sketch, "E2.21.5.0", {"center": v(25.4, -177.8) * mm, "radius": 8 * mm});
            skCircle(sketch, "E2.21.6.0", {"center": v(25.4, -127) * mm, "radius": 8 * mm});
            skCircle(sketch, "E2.21.7.0", {"center": v(25.4, -76.2) * mm, "radius": 8 * mm});
            skCircle(sketch, "E2.21.8.0", {"center": v(25.4, -25.4) * mm, "radius": 8 * mm});
            skCircle(sketch, "E2.21.9.0", {"center": v(25.4, 25.4) * mm, "radius": 8 * mm});
            skCircle(sketch, "E2.21.10.0", {"center": v(25.4, 76.2) * mm, "radius": 8 * mm});
            skCircle(sketch, "E2.21.11.0", {"center": v(25.4, 127) * mm, "radius": 8 * mm});
            skCircle(sketch, "E2.21.12.0", {"center": v(25.4, 177.8) * mm, "radius": 8 * mm});
            skCircle(sketch, "E2.21.13.0", {"center": v(25.4, 228.6) * mm, "radius": 8 * mm});
            skCircle(sketch, "E2.21.14.0", {"center": v(25.4, 279.4) * mm, "radius": 8 * mm});
            skCircle(sketch, "E2.21.15.0", {"center": v(25.4, 330.2) * mm, "radius": 8 * mm});
            skCircle(sketch, "E2.21.16.0", {"center": v(25.4, 381) * mm, "radius": 8 * mm});
            skCircle(sketch, "E2.21.17.0", {"center": v(25.4, 431.8) * mm, "radius": 8 * mm});
            skCircle(sketch, "E2.22.0.0", {"center": v(76.2, -431.8) * mm, "radius": 8 * mm});
            skCircle(sketch, "E2.22.1.0", {"center": v(76.2, -381) * mm, "radius": 8 * mm});
            skCircle(sketch, "E2.22.2.0", {"center": v(76.2, -330.2) * mm, "radius": 8 * mm});
            skCircle(sketch, "E2.22.3.0", {"center": v(76.2, -279.4) * mm, "radius": 8 * mm});
            skCircle(sketch, "E2.22.4.0", {"center": v(76.2, -228.6) * mm, "radius": 8 * mm});
            skCircle(sketch, "E2.22.5.0", {"center": v(76.2, -177.8) * mm, "radius": 8 * mm});
            skCircle(sketch, "E2.22.6.0", {"center": v(76.2, -127) * mm, "radius": 8 * mm});
            skCircle(sketch, "E2.22.7.0", {"center": v(76.2, -76.2) * mm, "radius": 8 * mm});
            skCircle(sketch, "E2.22.8.0", {"center": v(76.2, -25.4) * mm, "radius": 8 * mm});
            skCircle(sketch, "E2.22.9.0", {"center": v(76.2, 25.4) * mm, "radius": 8 * mm});
            skCircle(sketch, "E2.22.10.0", {"center": v(76.2, 76.2) * mm, "radius": 8 * mm});
            skCircle(sketch, "E2.22.11.0", {"center": v(76.2, 127) * mm, "radius": 8 * mm});
            skCircle(sketch, "E2.22.12.0", {"center": v(76.2, 177.8) * mm, "radius": 8 * mm});
            skCircle(sketch, "E2.22.13.0", {"center": v(76.2, 228.6) * mm, "radius": 8 * mm});
            skCircle(sketch, "E2.22.14.0", {"center": v(76.2, 279.4) * mm, "radius": 8 * mm});
            skCircle(sketch, "E2.22.15.0", {"center": v(76.2, 330.2) * mm, "radius": 8 * mm});
            skCircle(sketch, "E2.22.16.0", {"center": v(76.2, 381) * mm, "radius": 8 * mm});
            skCircle(sketch, "E2.22.17.0", {"center": v(76.2, 431.8) * mm, "radius": 8 * mm});
            skCircle(sketch, "E2.23.0.0", {"center": v(127, -431.8) * mm, "radius": 8 * mm});
            skCircle(sketch, "E2.23.1.0", {"center": v(127, -381) * mm, "radius": 8 * mm});
            skCircle(sketch, "E2.23.2.0", {"center": v(127, -330.2) * mm, "radius": 8 * mm});
            skCircle(sketch, "E2.23.3.0", {"center": v(127, -279.4) * mm, "radius": 8 * mm});
            skCircle(sketch, "E2.23.4.0", {"center": v(127, -228.6) * mm, "radius": 8 * mm});
            skCircle(sketch, "E2.23.5.0", {"center": v(127, -177.8) * mm, "radius": 8 * mm});
            skCircle(sketch, "E2.23.6.0", {"center": v(127, -127) * mm, "radius": 8 * mm});
            skCircle(sketch, "E2.23.7.0", {"center": v(127, -76.2) * mm, "radius": 8 * mm});
            skCircle(sketch, "E2.23.8.0", {"center": v(127, -25.4) * mm, "radius": 8 * mm});
            skCircle(sketch, "E2.23.9.0", {"center": v(127, 25.4) * mm, "radius": 8 * mm});
            skCircle(sketch, "E2.23.10.0", {"center": v(127, 76.2) * mm, "radius": 8 * mm});
            skCircle(sketch, "E2.23.11.0", {"center": v(127, 127) * mm, "radius": 8 * mm});
            skCircle(sketch, "E2.23.12.0", {"center": v(127, 177.8) * mm, "radius": 8 * mm});
            skCircle(sketch, "E2.23.13.0", {"center": v(127, 228.6) * mm, "radius": 8 * mm});
            skCircle(sketch, "E2.23.14.0", {"center": v(127, 279.4) * mm, "radius": 8 * mm});
            skCircle(sketch, "E2.23.15.0", {"center": v(127, 330.2) * mm, "radius": 8 * mm});
            skCircle(sketch, "E2.23.16.0", {"center": v(127, 381) * mm, "radius": 8 * mm});
            skCircle(sketch, "E2.23.17.0", {"center": v(127, 431.8) * mm, "radius": 8 * mm});
            skCircle(sketch, "E2.24.0.0", {"center": v(177.8, -431.8) * mm, "radius": 8 * mm});
            skCircle(sketch, "E2.24.1.0", {"center": v(177.8, -381) * mm, "radius": 8 * mm});
            skCircle(sketch, "E2.24.2.0", {"center": v(177.8, -330.2) * mm, "radius": 8 * mm});
            skCircle(sketch, "E2.24.3.0", {"center": v(177.8, -279.4) * mm, "radius": 8 * mm});
            skCircle(sketch, "E2.24.4.0", {"center": v(177.8, -228.6) * mm, "radius": 8 * mm});
            skCircle(sketch, "E2.24.5.0", {"center": v(177.8, -177.8) * mm, "radius": 8 * mm});
            skCircle(sketch, "E2.24.6.0", {"center": v(177.8, -127) * mm, "radius": 8 * mm});
            skCircle(sketch, "E2.24.7.0", {"center": v(177.8, -76.2) * mm, "radius": 8 * mm});
            skCircle(sketch, "E2.24.8.0", {"center": v(177.8, -25.4) * mm, "radius": 8 * mm});
            skCircle(sketch, "E2.24.9.0", {"center": v(177.8, 25.4) * mm, "radius": 8 * mm});
            skCircle(sketch, "E2.24.10.0", {"center": v(177.8, 76.2) * mm, "radius": 8 * mm});
            skCircle(sketch, "E2.24.11.0", {"center": v(177.8, 127) * mm, "radius": 8 * mm});
            skCircle(sketch, "E2.24.12.0", {"center": v(177.8, 177.8) * mm, "radius": 8 * mm});
            skCircle(sketch, "E2.24.13.0", {"center": v(177.8, 228.6) * mm, "radius": 8 * mm});
            skCircle(sketch, "E2.24.14.0", {"center": v(177.8, 279.4) * mm, "radius": 8 * mm});
            skCircle(sketch, "E2.24.15.0", {"center": v(177.8, 330.2) * mm, "radius": 8 * mm});
            skCircle(sketch, "E2.24.16.0", {"center": v(177.8, 381) * mm, "radius": 8 * mm});
            skCircle(sketch, "E2.24.17.0", {"center": v(177.8, 431.8) * mm, "radius": 8 * mm});
            skCircle(sketch, "E2.25.0.0", {"center": v(228.6, -431.8) * mm, "radius": 8 * mm});
            skCircle(sketch, "E2.25.1.0", {"center": v(228.6, -381) * mm, "radius": 8 * mm});
            skCircle(sketch, "E2.25.2.0", {"center": v(228.6, -330.2) * mm, "radius": 8 * mm});
            skCircle(sketch, "E2.25.3.0", {"center": v(228.6, -279.4) * mm, "radius": 8 * mm});
            skCircle(sketch, "E2.25.4.0", {"center": v(228.6, -228.6) * mm, "radius": 8 * mm});
            skCircle(sketch, "E2.25.5.0", {"center": v(228.6, -177.8) * mm, "radius": 8 * mm});
            skCircle(sketch, "E2.25.6.0", {"center": v(228.6, -127) * mm, "radius": 8 * mm});
            skCircle(sketch, "E2.25.7.0", {"center": v(228.6, -76.2) * mm, "radius": 8 * mm});
            skCircle(sketch, "E2.25.8.0", {"center": v(228.6, -25.4) * mm, "radius": 8 * mm});
            skCircle(sketch, "E2.25.9.0", {"center": v(228.6, 25.4) * mm, "radius": 8 * mm});
            skCircle(sketch, "E2.25.10.0", {"center": v(228.6, 76.2) * mm, "radius": 8 * mm});
            skCircle(sketch, "E2.25.11.0", {"center": v(228.6, 127) * mm, "radius": 8 * mm});
            skCircle(sketch, "E2.25.12.0", {"center": v(228.6, 177.8) * mm, "radius": 8 * mm});
            skCircle(sketch, "E2.25.13.0", {"center": v(228.6, 228.6) * mm, "radius": 8 * mm});
            skCircle(sketch, "E2.25.14.0", {"center": v(228.6, 279.4) * mm, "radius": 8 * mm});
            skCircle(sketch, "E2.25.15.0", {"center": v(228.6, 330.2) * mm, "radius": 8 * mm});
            skCircle(sketch, "E2.25.16.0", {"center": v(228.6, 381) * mm, "radius": 8 * mm});
            skCircle(sketch, "E2.25.17.0", {"center": v(228.6, 431.8) * mm, "radius": 8 * mm});
            skCircle(sketch, "E2.26.0.0", {"center": v(279.4, -431.8) * mm, "radius": 8 * mm});
            skCircle(sketch, "E2.26.1.0", {"center": v(279.4, -381) * mm, "radius": 8 * mm});
            skCircle(sketch, "E2.26.2.0", {"center": v(279.4, -330.2) * mm, "radius": 8 * mm});
            skCircle(sketch, "E2.26.3.0", {"center": v(279.4, -279.4) * mm, "radius": 8 * mm});
            skCircle(sketch, "E2.26.4.0", {"center": v(279.4, -228.6) * mm, "radius": 8 * mm});
            skCircle(sketch, "E2.26.5.0", {"center": v(279.4, -177.8) * mm, "radius": 8 * mm});
            skCircle(sketch, "E2.26.6.0", {"center": v(279.4, -127) * mm, "radius": 8 * mm});
            skCircle(sketch, "E2.26.7.0", {"center": v(279.4, -76.2) * mm, "radius": 8 * mm});
            skCircle(sketch, "E2.26.8.0", {"center": v(279.4, -25.4) * mm, "radius": 8 * mm});
            skCircle(sketch, "E2.26.9.0", {"center": v(279.4, 25.4) * mm, "radius": 8 * mm});
            skCircle(sketch, "E2.26.10.0", {"center": v(279.4, 76.2) * mm, "radius": 8 * mm});
            skCircle(sketch, "E2.26.11.0", {"center": v(279.4, 127) * mm, "radius": 8 * mm});
            skCircle(sketch, "E2.26.12.0", {"center": v(279.4, 177.8) * mm, "radius": 8 * mm});
            skCircle(sketch, "E2.26.13.0", {"center": v(279.4, 228.6) * mm, "radius": 8 * mm});
            skCircle(sketch, "E2.26.14.0", {"center": v(279.4, 279.4) * mm, "radius": 8 * mm});
            skCircle(sketch, "E2.26.15.0", {"center": v(279.4, 330.2) * mm, "radius": 8 * mm});
            skCircle(sketch, "E2.26.16.0", {"center": v(279.4, 381) * mm, "radius": 8 * mm});
            skCircle(sketch, "E2.26.17.0", {"center": v(279.4, 431.8) * mm, "radius": 8 * mm});
            skCircle(sketch, "E2.27.0.0", {"center": v(330.2, -431.8) * mm, "radius": 8 * mm});
            skCircle(sketch, "E2.27.1.0", {"center": v(330.2, -381) * mm, "radius": 8 * mm});
            skCircle(sketch, "E2.27.2.0", {"center": v(330.2, -330.2) * mm, "radius": 8 * mm});
            skCircle(sketch, "E2.27.3.0", {"center": v(330.2, -279.4) * mm, "radius": 8 * mm});
            skCircle(sketch, "E2.27.4.0", {"center": v(330.2, -228.6) * mm, "radius": 8 * mm});
            skCircle(sketch, "E2.27.5.0", {"center": v(330.2, -177.8) * mm, "radius": 8 * mm});
            skCircle(sketch, "E2.27.6.0", {"center": v(330.2, -127) * mm, "radius": 8 * mm});
            skCircle(sketch, "E2.27.7.0", {"center": v(330.2, -76.2) * mm, "radius": 8 * mm});
            skCircle(sketch, "E2.27.8.0", {"center": v(330.2, -25.4) * mm, "radius": 8 * mm});
            skCircle(sketch, "E2.27.9.0", {"center": v(330.2, 25.4) * mm, "radius": 8 * mm});
            skCircle(sketch, "E2.27.10.0", {"center": v(330.2, 76.2) * mm, "radius": 8 * mm});
            skCircle(sketch, "E2.27.11.0", {"center": v(330.2, 127) * mm, "radius": 8 * mm});
            skCircle(sketch, "E2.27.12.0", {"center": v(330.2, 177.8) * mm, "radius": 8 * mm});
            skCircle(sketch, "E2.27.13.0", {"center": v(330.2, 228.6) * mm, "radius": 8 * mm});
            skCircle(sketch, "E2.27.14.0", {"center": v(330.2, 279.4) * mm, "radius": 8 * mm});
            skCircle(sketch, "E2.27.15.0", {"center": v(330.2, 330.2) * mm, "radius": 8 * mm});
            skCircle(sketch, "E2.27.16.0", {"center": v(330.2, 381) * mm, "radius": 8 * mm});
            skCircle(sketch, "E2.27.17.0", {"center": v(330.2, 431.8) * mm, "radius": 8 * mm});
            skCircle(sketch, "E2.28.0.0", {"center": v(381, -431.8) * mm, "radius": 8 * mm});
            skCircle(sketch, "E2.28.1.0", {"center": v(381, -381) * mm, "radius": 8 * mm});
            skCircle(sketch, "E2.28.2.0", {"center": v(381, -330.2) * mm, "radius": 8 * mm});
            skCircle(sketch, "E2.28.3.0", {"center": v(381, -279.4) * mm, "radius": 8 * mm});
            skCircle(sketch, "E2.28.4.0", {"center": v(381, -228.6) * mm, "radius": 8 * mm});
            skCircle(sketch, "E2.28.5.0", {"center": v(381, -177.8) * mm, "radius": 8 * mm});
            skCircle(sketch, "E2.28.6.0", {"center": v(381, -127) * mm, "radius": 8 * mm});
            skCircle(sketch, "E2.28.7.0", {"center": v(381, -76.2) * mm, "radius": 8 * mm});
            skCircle(sketch, "E2.28.8.0", {"center": v(381, -25.4) * mm, "radius": 8 * mm});
            skCircle(sketch, "E2.28.9.0", {"center": v(381, 25.4) * mm, "radius": 8 * mm});
            skCircle(sketch, "E2.28.10.0", {"center": v(381, 76.2) * mm, "radius": 8 * mm});
            skCircle(sketch, "E2.28.11.0", {"center": v(381, 127) * mm, "radius": 8 * mm});
            skCircle(sketch, "E2.28.12.0", {"center": v(381, 177.8) * mm, "radius": 8 * mm});
            skCircle(sketch, "E2.28.13.0", {"center": v(381, 228.6) * mm, "radius": 8 * mm});
            skCircle(sketch, "E2.28.14.0", {"center": v(381, 279.4) * mm, "radius": 8 * mm});
            skCircle(sketch, "E2.28.15.0", {"center": v(381, 330.2) * mm, "radius": 8 * mm});
            skCircle(sketch, "E2.28.16.0", {"center": v(381, 381) * mm, "radius": 8 * mm});
            skCircle(sketch, "E2.28.17.0", {"center": v(381, 431.8) * mm, "radius": 8 * mm});
            skCircle(sketch, "E2.29.0.0", {"center": v(431.8, -431.8) * mm, "radius": 8 * mm});
            skCircle(sketch, "E2.29.1.0", {"center": v(431.8, -381) * mm, "radius": 8 * mm});
            skCircle(sketch, "E2.29.2.0", {"center": v(431.8, -330.2) * mm, "radius": 8 * mm});
            skCircle(sketch, "E2.29.3.0", {"center": v(431.8, -279.4) * mm, "radius": 8 * mm});
            skCircle(sketch, "E2.29.4.0", {"center": v(431.8, -228.6) * mm, "radius": 8 * mm});
            skCircle(sketch, "E2.29.5.0", {"center": v(431.8, -177.8) * mm, "radius": 8 * mm});
            skCircle(sketch, "E2.29.6.0", {"center": v(431.8, -127) * mm, "radius": 8 * mm});
            skCircle(sketch, "E2.29.7.0", {"center": v(431.8, -76.2) * mm, "radius": 8 * mm});
            skCircle(sketch, "E2.29.8.0", {"center": v(431.8, -25.4) * mm, "radius": 8 * mm});
            skCircle(sketch, "E2.29.9.0", {"center": v(431.8, 25.4) * mm, "radius": 8 * mm});
            skCircle(sketch, "E2.29.10.0", {"center": v(431.8, 76.2) * mm, "radius": 8 * mm});
            skCircle(sketch, "E2.29.11.0", {"center": v(431.8, 127) * mm, "radius": 8 * mm});
            skCircle(sketch, "E2.29.12.0", {"center": v(431.8, 177.8) * mm, "radius": 8 * mm});
            skCircle(sketch, "E2.29.13.0", {"center": v(431.8, 228.6) * mm, "radius": 8 * mm});
            skCircle(sketch, "E2.29.14.0", {"center": v(431.8, 279.4) * mm, "radius": 8 * mm});
            skCircle(sketch, "E2.29.15.0", {"center": v(431.8, 330.2) * mm, "radius": 8 * mm});
            skCircle(sketch, "E2.29.16.0", {"center": v(431.8, 381) * mm, "radius": 8 * mm});
            skCircle(sketch, "E2.29.17.0", {"center": v(431.8, 431.8) * mm, "radius": 8 * mm});
            skCircle(sketch, "E2.30.0.0", {"center": v(482.6, -431.8) * mm, "radius": 8 * mm});
            skCircle(sketch, "E2.30.1.0", {"center": v(482.6, -381) * mm, "radius": 8 * mm});
            skCircle(sketch, "E2.30.2.0", {"center": v(482.6, -330.2) * mm, "radius": 8 * mm});
            skCircle(sketch, "E2.30.3.0", {"center": v(482.6, -279.4) * mm, "radius": 8 * mm});
            skCircle(sketch, "E2.30.4.0", {"center": v(482.6, -228.6) * mm, "radius": 8 * mm});
            skCircle(sketch, "E2.30.5.0", {"center": v(482.6, -177.8) * mm, "radius": 8 * mm});
            skCircle(sketch, "E2.30.6.0", {"center": v(482.6, -127) * mm, "radius": 8 * mm});
            skCircle(sketch, "E2.30.7.0", {"center": v(482.6, -76.2) * mm, "radius": 8 * mm});
            skCircle(sketch, "E2.30.8.0", {"center": v(482.6, -25.4) * mm, "radius": 8 * mm});
            skCircle(sketch, "E2.30.9.0", {"center": v(482.6, 25.4) * mm, "radius": 8 * mm});
            skCircle(sketch, "E2.30.10.0", {"center": v(482.6, 76.2) * mm, "radius": 8 * mm});
            skCircle(sketch, "E2.30.11.0", {"center": v(482.6, 127) * mm, "radius": 8 * mm});
            skCircle(sketch, "E2.30.12.0", {"center": v(482.6, 177.8) * mm, "radius": 8 * mm});
            skCircle(sketch, "E2.30.13.0", {"center": v(482.6, 228.6) * mm, "radius": 8 * mm});
            skCircle(sketch, "E2.30.14.0", {"center": v(482.6, 279.4) * mm, "radius": 8 * mm});
            skCircle(sketch, "E2.30.15.0", {"center": v(482.6, 330.2) * mm, "radius": 8 * mm});
            skCircle(sketch, "E2.30.16.0", {"center": v(482.6, 381) * mm, "radius": 8 * mm});
            skCircle(sketch, "E2.30.17.0", {"center": v(482.6, 431.8) * mm, "radius": 8 * mm});
            skCircle(sketch, "E2.31.0.0", {"center": v(533.4, -431.8) * mm, "radius": 8 * mm});
            skCircle(sketch, "E2.31.1.0", {"center": v(533.4, -381) * mm, "radius": 8 * mm});
            skCircle(sketch, "E2.31.2.0", {"center": v(533.4, -330.2) * mm, "radius": 8 * mm});
            skCircle(sketch, "E2.31.3.0", {"center": v(533.4, -279.4) * mm, "radius": 8 * mm});
            skCircle(sketch, "E2.31.4.0", {"center": v(533.4, -228.6) * mm, "radius": 8 * mm});
            skCircle(sketch, "E2.31.5.0", {"center": v(533.4, -177.8) * mm, "radius": 8 * mm});
            skCircle(sketch, "E2.31.6.0", {"center": v(533.4, -127) * mm, "radius": 8 * mm});
            skCircle(sketch, "E2.31.7.0", {"center": v(533.4, -76.2) * mm, "radius": 8 * mm});
            skCircle(sketch, "E2.31.8.0", {"center": v(533.4, -25.4) * mm, "radius": 8 * mm});
            skCircle(sketch, "E2.31.9.0", {"center": v(533.4, 25.4) * mm, "radius": 8 * mm});
            skCircle(sketch, "E2.31.10.0", {"center": v(533.4, 76.2) * mm, "radius": 8 * mm});
            skCircle(sketch, "E2.31.11.0", {"center": v(533.4, 127) * mm, "radius": 8 * mm});
            skCircle(sketch, "E2.31.12.0", {"center": v(533.4, 177.8) * mm, "radius": 8 * mm});
            skCircle(sketch, "E2.31.13.0", {"center": v(533.4, 228.6) * mm, "radius": 8 * mm});
            skCircle(sketch, "E2.31.14.0", {"center": v(533.4, 279.4) * mm, "radius": 8 * mm});
            skCircle(sketch, "E2.31.15.0", {"center": v(533.4, 330.2) * mm, "radius": 8 * mm});
            skCircle(sketch, "E2.31.16.0", {"center": v(533.4, 381) * mm, "radius": 8 * mm});
            skCircle(sketch, "E2.31.17.0", {"center": v(533.4, 431.8) * mm, "radius": 8 * mm});
            skCircle(sketch, "E2.32.0.0", {"center": v(584.2, -431.8) * mm, "radius": 8 * mm});
            skCircle(sketch, "E2.32.1.0", {"center": v(584.2, -381) * mm, "radius": 8 * mm});
            skCircle(sketch, "E2.32.2.0", {"center": v(584.2, -330.2) * mm, "radius": 8 * mm});
            skCircle(sketch, "E2.32.3.0", {"center": v(584.2, -279.4) * mm, "radius": 8 * mm});
            skCircle(sketch, "E2.32.4.0", {"center": v(584.2, -228.6) * mm, "radius": 8 * mm});
            skCircle(sketch, "E2.32.5.0", {"center": v(584.2, -177.8) * mm, "radius": 8 * mm});
            skCircle(sketch, "E2.32.6.0", {"center": v(584.2, -127) * mm, "radius": 8 * mm});
            skCircle(sketch, "E2.32.7.0", {"center": v(584.2, -76.2) * mm, "radius": 8 * mm});
            skCircle(sketch, "E2.32.8.0", {"center": v(584.2, -25.4) * mm, "radius": 8 * mm});
            skCircle(sketch, "E2.32.9.0", {"center": v(584.2, 25.4) * mm, "radius": 8 * mm});
            skCircle(sketch, "E2.32.10.0", {"center": v(584.2, 76.2) * mm, "radius": 8 * mm});
            skCircle(sketch, "E2.32.11.0", {"center": v(584.2, 127) * mm, "radius": 8 * mm});
            skCircle(sketch, "E2.32.12.0", {"center": v(584.2, 177.8) * mm, "radius": 8 * mm});
            skCircle(sketch, "E2.32.13.0", {"center": v(584.2, 228.6) * mm, "radius": 8 * mm});
            skCircle(sketch, "E2.32.14.0", {"center": v(584.2, 279.4) * mm, "radius": 8 * mm});
            skCircle(sketch, "E2.32.15.0", {"center": v(584.2, 330.2) * mm, "radius": 8 * mm});
            skCircle(sketch, "E2.32.16.0", {"center": v(584.2, 381) * mm, "radius": 8 * mm});
            skCircle(sketch, "E2.32.17.0", {"center": v(584.2, 431.8) * mm, "radius": 8 * mm});
            skCircle(sketch, "E2.33.0.0", {"center": v(635, -431.8) * mm, "radius": 8 * mm});
            skCircle(sketch, "E2.33.1.0", {"center": v(635, -381) * mm, "radius": 8 * mm});
            skCircle(sketch, "E2.33.2.0", {"center": v(635, -330.2) * mm, "radius": 8 * mm});
            skCircle(sketch, "E2.33.3.0", {"center": v(635, -279.4) * mm, "radius": 8 * mm});
            skCircle(sketch, "E2.33.4.0", {"center": v(635, -228.6) * mm, "radius": 8 * mm});
            skCircle(sketch, "E2.33.5.0", {"center": v(635, -177.8) * mm, "radius": 8 * mm});
            skCircle(sketch, "E2.33.6.0", {"center": v(635, -127) * mm, "radius": 8 * mm});
            skCircle(sketch, "E2.33.7.0", {"center": v(635, -76.2) * mm, "radius": 8 * mm});
            skCircle(sketch, "E2.33.8.0", {"center": v(635, -25.4) * mm, "radius": 8 * mm});
            skCircle(sketch, "E2.33.9.0", {"center": v(635, 25.4) * mm, "radius": 8 * mm});
            skCircle(sketch, "E2.33.10.0", {"center": v(635, 76.2) * mm, "radius": 8 * mm});
            skCircle(sketch, "E2.33.11.0", {"center": v(635, 127) * mm, "radius": 8 * mm});
            skCircle(sketch, "E2.33.12.0", {"center": v(635, 177.8) * mm, "radius": 8 * mm});
            skCircle(sketch, "E2.33.13.0", {"center": v(635, 228.6) * mm, "radius": 8 * mm});
            skCircle(sketch, "E2.33.14.0", {"center": v(635, 279.4) * mm, "radius": 8 * mm});
            skCircle(sketch, "E2.33.15.0", {"center": v(635, 330.2) * mm, "radius": 8 * mm});
            skCircle(sketch, "E2.33.16.0", {"center": v(635, 381) * mm, "radius": 8 * mm});
            skCircle(sketch, "E2.33.17.0", {"center": v(635, 431.8) * mm, "radius": 8 * mm});
            skCircle(sketch, "E2.34.0.0", {"center": v(685.8, -431.8) * mm, "radius": 8 * mm});
            skCircle(sketch, "E2.34.1.0", {"center": v(685.8, -381) * mm, "radius": 8 * mm});
            skCircle(sketch, "E2.34.2.0", {"center": v(685.8, -330.2) * mm, "radius": 8 * mm});
            skCircle(sketch, "E2.34.3.0", {"center": v(685.8, -279.4) * mm, "radius": 8 * mm});
            skCircle(sketch, "E2.34.4.0", {"center": v(685.8, -228.6) * mm, "radius": 8 * mm});
            skCircle(sketch, "E2.34.5.0", {"center": v(685.8, -177.8) * mm, "radius": 8 * mm});
            skCircle(sketch, "E2.34.6.0", {"center": v(685.8, -127) * mm, "radius": 8 * mm});
            skCircle(sketch, "E2.34.7.0", {"center": v(685.8, -76.2) * mm, "radius": 8 * mm});
            skCircle(sketch, "E2.34.8.0", {"center": v(685.8, -25.4) * mm, "radius": 8 * mm});
            skCircle(sketch, "E2.34.9.0", {"center": v(685.8, 25.4) * mm, "radius": 8 * mm});
            skCircle(sketch, "E2.34.10.0", {"center": v(685.8, 76.2) * mm, "radius": 8 * mm});
            skCircle(sketch, "E2.34.11.0", {"center": v(685.8, 127) * mm, "radius": 8 * mm});
            skCircle(sketch, "E2.34.12.0", {"center": v(685.8, 177.8) * mm, "radius": 8 * mm});
            skCircle(sketch, "E2.34.13.0", {"center": v(685.8, 228.6) * mm, "radius": 8 * mm});
            skCircle(sketch, "E2.34.14.0", {"center": v(685.8, 279.4) * mm, "radius": 8 * mm});
            skCircle(sketch, "E2.34.15.0", {"center": v(685.8, 330.2) * mm, "radius": 8 * mm});
            skCircle(sketch, "E2.34.16.0", {"center": v(685.8, 381) * mm, "radius": 8 * mm});
            skCircle(sketch, "E2.34.17.0", {"center": v(685.8, 431.8) * mm, "radius": 8 * mm});
            skCircle(sketch, "E2.35.0.0", {"center": v(736.6, -431.8) * mm, "radius": 8 * mm});
            skCircle(sketch, "E2.35.1.0", {"center": v(736.6, -381) * mm, "radius": 8 * mm});
            skCircle(sketch, "E2.35.2.0", {"center": v(736.6, -330.2) * mm, "radius": 8 * mm});
            skCircle(sketch, "E2.35.3.0", {"center": v(736.6, -279.4) * mm, "radius": 8 * mm});
            skCircle(sketch, "E2.35.4.0", {"center": v(736.6, -228.6) * mm, "radius": 8 * mm});
            skCircle(sketch, "E2.35.5.0", {"center": v(736.6, -177.8) * mm, "radius": 8 * mm});
            skCircle(sketch, "E2.35.6.0", {"center": v(736.6, -127) * mm, "radius": 8 * mm});
            skCircle(sketch, "E2.35.7.0", {"center": v(736.6, -76.2) * mm, "radius": 8 * mm});
            skCircle(sketch, "E2.35.8.0", {"center": v(736.6, -25.4) * mm, "radius": 8 * mm});
            skCircle(sketch, "E2.35.9.0", {"center": v(736.6, 25.4) * mm, "radius": 8 * mm});
            skCircle(sketch, "E2.35.10.0", {"center": v(736.6, 76.2) * mm, "radius": 8 * mm});
            skCircle(sketch, "E2.35.11.0", {"center": v(736.6, 127) * mm, "radius": 8 * mm});
            skCircle(sketch, "E2.35.12.0", {"center": v(736.6, 177.8) * mm, "radius": 8 * mm});
            skCircle(sketch, "E2.35.13.0", {"center": v(736.6, 228.6) * mm, "radius": 8 * mm});
            skCircle(sketch, "E2.35.14.0", {"center": v(736.6, 279.4) * mm, "radius": 8 * mm});
            skCircle(sketch, "E2.35.15.0", {"center": v(736.6, 330.2) * mm, "radius": 8 * mm});
            skCircle(sketch, "E2.35.16.0", {"center": v(736.6, 381) * mm, "radius": 8 * mm});
            skCircle(sketch, "E2.35.17.0", {"center": v(736.6, 431.8) * mm, "radius": 8 * mm});
            skCircle(sketch, "E2.36.0.0", {"center": v(787.4, -431.8) * mm, "radius": 8 * mm});
            skCircle(sketch, "E2.36.1.0", {"center": v(787.4, -381) * mm, "radius": 8 * mm});
            skCircle(sketch, "E2.36.2.0", {"center": v(787.4, -330.2) * mm, "radius": 8 * mm});
            skCircle(sketch, "E2.36.3.0", {"center": v(787.4, -279.4) * mm, "radius": 8 * mm});
            skCircle(sketch, "E2.36.4.0", {"center": v(787.4, -228.6) * mm, "radius": 8 * mm});
            skCircle(sketch, "E2.36.5.0", {"center": v(787.4, -177.8) * mm, "radius": 8 * mm});
            skCircle(sketch, "E2.36.6.0", {"center": v(787.4, -127) * mm, "radius": 8 * mm});
            skCircle(sketch, "E2.36.7.0", {"center": v(787.4, -76.2) * mm, "radius": 8 * mm});
            skCircle(sketch, "E2.36.8.0", {"center": v(787.4, -25.4) * mm, "radius": 8 * mm});
            skCircle(sketch, "E2.36.9.0", {"center": v(787.4, 25.4) * mm, "radius": 8 * mm});
            skCircle(sketch, "E2.36.10.0", {"center": v(787.4, 76.2) * mm, "radius": 8 * mm});
            skCircle(sketch, "E2.36.11.0", {"center": v(787.4, 127) * mm, "radius": 8 * mm});
            skCircle(sketch, "E2.36.12.0", {"center": v(787.4, 177.8) * mm, "radius": 8 * mm});
            skCircle(sketch, "E2.36.13.0", {"center": v(787.4, 228.6) * mm, "radius": 8 * mm});
            skCircle(sketch, "E2.36.14.0", {"center": v(787.4, 279.4) * mm, "radius": 8 * mm});
            skCircle(sketch, "E2.36.15.0", {"center": v(787.4, 330.2) * mm, "radius": 8 * mm});
            skCircle(sketch, "E2.36.16.0", {"center": v(787.4, 381) * mm, "radius": 8 * mm});
            skCircle(sketch, "E2.36.17.0", {"center": v(787.4, 431.8) * mm, "radius": 8 * mm});
            skCircle(sketch, "E2.37.0.0", {"center": v(838.2, -431.8) * mm, "radius": 8 * mm});
            skCircle(sketch, "E2.37.1.0", {"center": v(838.2, -381) * mm, "radius": 8 * mm});
            skCircle(sketch, "E2.37.2.0", {"center": v(838.2, -330.2) * mm, "radius": 8 * mm});
            skCircle(sketch, "E2.37.3.0", {"center": v(838.2, -279.4) * mm, "radius": 8 * mm});
            skCircle(sketch, "E2.37.4.0", {"center": v(838.2, -228.6) * mm, "radius": 8 * mm});
            skCircle(sketch, "E2.37.5.0", {"center": v(838.2, -177.8) * mm, "radius": 8 * mm});
            skCircle(sketch, "E2.37.6.0", {"center": v(838.2, -127) * mm, "radius": 8 * mm});
            skCircle(sketch, "E2.37.7.0", {"center": v(838.2, -76.2) * mm, "radius": 8 * mm});
            skCircle(sketch, "E2.37.8.0", {"center": v(838.2, -25.4) * mm, "radius": 8 * mm});
            skCircle(sketch, "E2.37.9.0", {"center": v(838.2, 25.4) * mm, "radius": 8 * mm});
            skCircle(sketch, "E2.37.10.0", {"center": v(838.2, 76.2) * mm, "radius": 8 * mm});
            skCircle(sketch, "E2.37.11.0", {"center": v(838.2, 127) * mm, "radius": 8 * mm});
            skCircle(sketch, "E2.37.12.0", {"center": v(838.2, 177.8) * mm, "radius": 8 * mm});
            skCircle(sketch, "E2.37.13.0", {"center": v(838.2, 228.6) * mm, "radius": 8 * mm});
            skCircle(sketch, "E2.37.14.0", {"center": v(838.2, 279.4) * mm, "radius": 8 * mm});
            skCircle(sketch, "E2.37.15.0", {"center": v(838.2, 330.2) * mm, "radius": 8 * mm});
            skCircle(sketch, "E2.37.16.0", {"center": v(838.2, 381) * mm, "radius": 8 * mm});
            skCircle(sketch, "E2.37.17.0", {"center": v(838.2, 431.8) * mm, "radius": 8 * mm});
            skCircle(sketch, "E2.38.0.0", {"center": v(889, -431.8) * mm, "radius": 8 * mm});
            skCircle(sketch, "E2.38.1.0", {"center": v(889, -381) * mm, "radius": 8 * mm});
            skCircle(sketch, "E2.38.2.0", {"center": v(889, -330.2) * mm, "radius": 8 * mm});
            skCircle(sketch, "E2.38.3.0", {"center": v(889, -279.4) * mm, "radius": 8 * mm});
            skCircle(sketch, "E2.38.4.0", {"center": v(889, -228.6) * mm, "radius": 8 * mm});
            skCircle(sketch, "E2.38.5.0", {"center": v(889, -177.8) * mm, "radius": 8 * mm});
            skCircle(sketch, "E2.38.6.0", {"center": v(889, -127) * mm, "radius": 8 * mm});
            skCircle(sketch, "E2.38.7.0", {"center": v(889, -76.2) * mm, "radius": 8 * mm});
            skCircle(sketch, "E2.38.8.0", {"center": v(889, -25.4) * mm, "radius": 8 * mm});
            skCircle(sketch, "E2.38.9.0", {"center": v(889, 25.4) * mm, "radius": 8 * mm});
            skCircle(sketch, "E2.38.10.0", {"center": v(889, 76.2) * mm, "radius": 8 * mm});
            skCircle(sketch, "E2.38.11.0", {"center": v(889, 127) * mm, "radius": 8 * mm});
            skCircle(sketch, "E2.38.12.0", {"center": v(889, 177.8) * mm, "radius": 8 * mm});
            skCircle(sketch, "E2.38.13.0", {"center": v(889, 228.6) * mm, "radius": 8 * mm});
            skCircle(sketch, "E2.38.14.0", {"center": v(889, 279.4) * mm, "radius": 8 * mm});
            skCircle(sketch, "E2.38.15.0", {"center": v(889, 330.2) * mm, "radius": 8 * mm});
            skCircle(sketch, "E2.38.16.0", {"center": v(889, 381) * mm, "radius": 8 * mm});
            skCircle(sketch, "E2.38.17.0", {"center": v(889, 431.8) * mm, "radius": 8 * mm});
            skCircle(sketch, "E2.39.0.0", {"center": v(939.8, -431.8) * mm, "radius": 8 * mm});
            skCircle(sketch, "E2.39.1.0", {"center": v(939.8, -381) * mm, "radius": 8 * mm});
            skCircle(sketch, "E2.39.2.0", {"center": v(939.8, -330.2) * mm, "radius": 8 * mm});
            skCircle(sketch, "E2.39.3.0", {"center": v(939.8, -279.4) * mm, "radius": 8 * mm});
            skCircle(sketch, "E2.39.4.0", {"center": v(939.8, -228.6) * mm, "radius": 8 * mm});
            skCircle(sketch, "E2.39.5.0", {"center": v(939.8, -177.8) * mm, "radius": 8 * mm});
            skCircle(sketch, "E2.39.6.0", {"center": v(939.8, -127) * mm, "radius": 8 * mm});
            skCircle(sketch, "E2.39.7.0", {"center": v(939.8, -76.2) * mm, "radius": 8 * mm});
            skCircle(sketch, "E2.39.8.0", {"center": v(939.8, -25.4) * mm, "radius": 8 * mm});
            skCircle(sketch, "E2.39.9.0", {"center": v(939.8, 25.4) * mm, "radius": 8 * mm});
            skCircle(sketch, "E2.39.10.0", {"center": v(939.8, 76.2) * mm, "radius": 8 * mm});
            skCircle(sketch, "E2.39.11.0", {"center": v(939.8, 127) * mm, "radius": 8 * mm});
            skCircle(sketch, "E2.39.12.0", {"center": v(939.8, 177.8) * mm, "radius": 8 * mm});
            skCircle(sketch, "E2.39.13.0", {"center": v(939.8, 228.6) * mm, "radius": 8 * mm});
            skCircle(sketch, "E2.39.14.0", {"center": v(939.8, 279.4) * mm, "radius": 8 * mm});
            skCircle(sketch, "E2.39.15.0", {"center": v(939.8, 330.2) * mm, "radius": 8 * mm});
            skCircle(sketch, "E2.39.16.0", {"center": v(939.8, 381) * mm, "radius": 8 * mm});
            skCircle(sketch, "E2.39.17.0", {"center": v(939.8, 431.8) * mm, "radius": 8 * mm});
            skCircle(sketch, "E2.40.0.0", {"center": v(990.6, -431.8) * mm, "radius": 8 * mm});
            skCircle(sketch, "E2.40.1.0", {"center": v(990.6, -381) * mm, "radius": 8 * mm});
            skCircle(sketch, "E2.40.2.0", {"center": v(990.6, -330.2) * mm, "radius": 8 * mm});
            skCircle(sketch, "E2.40.3.0", {"center": v(990.6, -279.4) * mm, "radius": 8 * mm});
            skCircle(sketch, "E2.40.4.0", {"center": v(990.6, -228.6) * mm, "radius": 8 * mm});
            skCircle(sketch, "E2.40.5.0", {"center": v(990.6, -177.8) * mm, "radius": 8 * mm});
            skCircle(sketch, "E2.40.6.0", {"center": v(990.6, -127) * mm, "radius": 8 * mm});
            skCircle(sketch, "E2.40.7.0", {"center": v(990.6, -76.2) * mm, "radius": 8 * mm});
            skCircle(sketch, "E2.40.8.0", {"center": v(990.6, -25.4) * mm, "radius": 8 * mm});
            skCircle(sketch, "E2.40.9.0", {"center": v(990.6, 25.4) * mm, "radius": 8 * mm});
            skCircle(sketch, "E2.40.10.0", {"center": v(990.6, 76.2) * mm, "radius": 8 * mm});
            skCircle(sketch, "E2.40.11.0", {"center": v(990.6, 127) * mm, "radius": 8 * mm});
            skCircle(sketch, "E2.40.12.0", {"center": v(990.6, 177.8) * mm, "radius": 8 * mm});
            skCircle(sketch, "E2.40.13.0", {"center": v(990.6, 228.6) * mm, "radius": 8 * mm});
            skCircle(sketch, "E2.40.14.0", {"center": v(990.6, 279.4) * mm, "radius": 8 * mm});
            skCircle(sketch, "E2.40.15.0", {"center": v(990.6, 330.2) * mm, "radius": 8 * mm});
            skCircle(sketch, "E2.40.16.0", {"center": v(990.6, 381) * mm, "radius": 8 * mm});
            skCircle(sketch, "E2.40.17.0", {"center": v(990.6, 431.8) * mm, "radius": 8 * mm});
            skCircle(sketch, "E2.41.0.0", {"center": v(1041.4, -431.8) * mm, "radius": 8 * mm});
            skCircle(sketch, "E2.41.1.0", {"center": v(1041.4, -381) * mm, "radius": 8 * mm});
            skCircle(sketch, "E2.41.2.0", {"center": v(1041.4, -330.2) * mm, "radius": 8 * mm});
            skCircle(sketch, "E2.41.3.0", {"center": v(1041.4, -279.4) * mm, "radius": 8 * mm});
            skCircle(sketch, "E2.41.4.0", {"center": v(1041.4, -228.6) * mm, "radius": 8 * mm});
            skCircle(sketch, "E2.41.5.0", {"center": v(1041.4, -177.8) * mm, "radius": 8 * mm});
            skCircle(sketch, "E2.41.6.0", {"center": v(1041.4, -127) * mm, "radius": 8 * mm});
            skCircle(sketch, "E2.41.7.0", {"center": v(1041.4, -76.2) * mm, "radius": 8 * mm});
            skCircle(sketch, "E2.41.8.0", {"center": v(1041.4, -25.4) * mm, "radius": 8 * mm});
            skCircle(sketch, "E2.41.9.0", {"center": v(1041.4, 25.4) * mm, "radius": 8 * mm});
            skCircle(sketch, "E2.41.10.0", {"center": v(1041.4, 76.2) * mm, "radius": 8 * mm});
            skCircle(sketch, "E2.41.11.0", {"center": v(1041.4, 127) * mm, "radius": 8 * mm});
            skCircle(sketch, "E2.41.12.0", {"center": v(1041.4, 177.8) * mm, "radius": 8 * mm});
            skCircle(sketch, "E2.41.13.0", {"center": v(1041.4, 228.6) * mm, "radius": 8 * mm});
            skCircle(sketch, "E2.41.14.0", {"center": v(1041.4, 279.4) * mm, "radius": 8 * mm});
            skCircle(sketch, "E2.41.15.0", {"center": v(1041.4, 330.2) * mm, "radius": 8 * mm});
            skCircle(sketch, "E2.41.16.0", {"center": v(1041.4, 381) * mm, "radius": 8 * mm});
            skCircle(sketch, "E2.41.17.0", {"center": v(1041.4, 431.8) * mm, "radius": 8 * mm});
            skCircle(sketch, "E2.42.0.0", {"center": v(1092.2, -431.8) * mm, "radius": 8 * mm});
            skCircle(sketch, "E2.42.1.0", {"center": v(1092.2, -381) * mm, "radius": 8 * mm});
            skCircle(sketch, "E2.42.2.0", {"center": v(1092.2, -330.2) * mm, "radius": 8 * mm});
            skCircle(sketch, "E2.42.3.0", {"center": v(1092.2, -279.4) * mm, "radius": 8 * mm});
            skCircle(sketch, "E2.42.4.0", {"center": v(1092.2, -228.6) * mm, "radius": 8 * mm});
            skCircle(sketch, "E2.42.5.0", {"center": v(1092.2, -177.8) * mm, "radius": 8 * mm});
            skCircle(sketch, "E2.42.6.0", {"center": v(1092.2, -127) * mm, "radius": 8 * mm});
            skCircle(sketch, "E2.42.7.0", {"center": v(1092.2, -76.2) * mm, "radius": 8 * mm});
            skCircle(sketch, "E2.42.8.0", {"center": v(1092.2, -25.4) * mm, "radius": 8 * mm});
            skCircle(sketch, "E2.42.9.0", {"center": v(1092.2, 25.4) * mm, "radius": 8 * mm});
            skCircle(sketch, "E2.42.10.0", {"center": v(1092.2, 76.2) * mm, "radius": 8 * mm});
            skCircle(sketch, "E2.42.11.0", {"center": v(1092.2, 127) * mm, "radius": 8 * mm});
            skCircle(sketch, "E2.42.12.0", {"center": v(1092.2, 177.8) * mm, "radius": 8 * mm});
            skCircle(sketch, "E2.42.13.0", {"center": v(1092.2, 228.6) * mm, "radius": 8 * mm});
            skCircle(sketch, "E2.42.14.0", {"center": v(1092.2, 279.4) * mm, "radius": 8 * mm});
            skCircle(sketch, "E2.42.15.0", {"center": v(1092.2, 330.2) * mm, "radius": 8 * mm});
            skCircle(sketch, "E2.42.16.0", {"center": v(1092.2, 381) * mm, "radius": 8 * mm});
            skCircle(sketch, "E2.42.17.0", {"center": v(1092.2, 431.8) * mm, "radius": 8 * mm});
            skCircle(sketch, "E2.43.0.0", {"center": v(1143, -431.8) * mm, "radius": 8 * mm});
            skCircle(sketch, "E2.43.1.0", {"center": v(1143, -381) * mm, "radius": 8 * mm});
            skCircle(sketch, "E2.43.2.0", {"center": v(1143, -330.2) * mm, "radius": 8 * mm});
            skCircle(sketch, "E2.43.3.0", {"center": v(1143, -279.4) * mm, "radius": 8 * mm});
            skCircle(sketch, "E2.43.4.0", {"center": v(1143, -228.6) * mm, "radius": 8 * mm});
            skCircle(sketch, "E2.43.5.0", {"center": v(1143, -177.8) * mm, "radius": 8 * mm});
            skCircle(sketch, "E2.43.6.0", {"center": v(1143, -127) * mm, "radius": 8 * mm});
            skCircle(sketch, "E2.43.7.0", {"center": v(1143, -76.2) * mm, "radius": 8 * mm});
            skCircle(sketch, "E2.43.8.0", {"center": v(1143, -25.4) * mm, "radius": 8 * mm});
            skCircle(sketch, "E2.43.9.0", {"center": v(1143, 25.4) * mm, "radius": 8 * mm});
            skCircle(sketch, "E2.43.10.0", {"center": v(1143, 76.2) * mm, "radius": 8 * mm});
            skCircle(sketch, "E2.43.11.0", {"center": v(1143, 127) * mm, "radius": 8 * mm});
            skCircle(sketch, "E2.43.12.0", {"center": v(1143, 177.8) * mm, "radius": 8 * mm});
            skCircle(sketch, "E2.43.13.0", {"center": v(1143, 228.6) * mm, "radius": 8 * mm});
            skCircle(sketch, "E2.43.14.0", {"center": v(1143, 279.4) * mm, "radius": 8 * mm});
            skCircle(sketch, "E2.43.15.0", {"center": v(1143, 330.2) * mm, "radius": 8 * mm});
            skCircle(sketch, "E2.43.16.0", {"center": v(1143, 381) * mm, "radius": 8 * mm});
            skCircle(sketch, "E2.43.17.0", {"center": v(1143, 431.8) * mm, "radius": 8 * mm});
            skCircle(sketch, "E2.44.0.0", {"center": v(1193.8, -431.8) * mm, "radius": 8 * mm});
            skCircle(sketch, "E2.44.1.0", {"center": v(1193.8, -381) * mm, "radius": 8 * mm});
            skCircle(sketch, "E2.44.2.0", {"center": v(1193.8, -330.2) * mm, "radius": 8 * mm});
            skCircle(sketch, "E2.44.3.0", {"center": v(1193.8, -279.4) * mm, "radius": 8 * mm});
            skCircle(sketch, "E2.44.4.0", {"center": v(1193.8, -228.6) * mm, "radius": 8 * mm});
            skCircle(sketch, "E2.44.5.0", {"center": v(1193.8, -177.8) * mm, "radius": 8 * mm});
            skCircle(sketch, "E2.44.6.0", {"center": v(1193.8, -127) * mm, "radius": 8 * mm});
            skCircle(sketch, "E2.44.7.0", {"center": v(1193.8, -76.2) * mm, "radius": 8 * mm});
            skCircle(sketch, "E2.44.8.0", {"center": v(1193.8, -25.4) * mm, "radius": 8 * mm});
            skCircle(sketch, "E2.44.9.0", {"center": v(1193.8, 25.4) * mm, "radius": 8 * mm});
            skCircle(sketch, "E2.44.10.0", {"center": v(1193.8, 76.2) * mm, "radius": 8 * mm});
            skCircle(sketch, "E2.44.11.0", {"center": v(1193.8, 127) * mm, "radius": 8 * mm});
            skCircle(sketch, "E2.44.12.0", {"center": v(1193.8, 177.8) * mm, "radius": 8 * mm});
            skCircle(sketch, "E2.44.13.0", {"center": v(1193.8, 228.6) * mm, "radius": 8 * mm});
            skCircle(sketch, "E2.44.14.0", {"center": v(1193.8, 279.4) * mm, "radius": 8 * mm});
            skCircle(sketch, "E2.44.15.0", {"center": v(1193.8, 330.2) * mm, "radius": 8 * mm});
            skCircle(sketch, "E2.44.16.0", {"center": v(1193.8, 381) * mm, "radius": 8 * mm});
            skCircle(sketch, "E2.44.17.0", {"center": v(1193.8, 431.8) * mm, "radius": 8 * mm});
            skCircle(sketch, "E2.45.0.0", {"center": v(1244.6, -431.8) * mm, "radius": 8 * mm});
            skCircle(sketch, "E2.45.1.0", {"center": v(1244.6, -381) * mm, "radius": 8 * mm});
            skCircle(sketch, "E2.45.2.0", {"center": v(1244.6, -330.2) * mm, "radius": 8 * mm});
            skCircle(sketch, "E2.45.3.0", {"center": v(1244.6, -279.4) * mm, "radius": 8 * mm});
            skCircle(sketch, "E2.45.4.0", {"center": v(1244.6, -228.6) * mm, "radius": 8 * mm});
            skCircle(sketch, "E2.45.5.0", {"center": v(1244.6, -177.8) * mm, "radius": 8 * mm});
            skCircle(sketch, "E2.45.6.0", {"center": v(1244.6, -127) * mm, "radius": 8 * mm});
            skCircle(sketch, "E2.45.7.0", {"center": v(1244.6, -76.2) * mm, "radius": 8 * mm});
            skCircle(sketch, "E2.45.8.0", {"center": v(1244.6, -25.4) * mm, "radius": 8 * mm});
            skCircle(sketch, "E2.45.9.0", {"center": v(1244.6, 25.4) * mm, "radius": 8 * mm});
            skCircle(sketch, "E2.45.10.0", {"center": v(1244.6, 76.2) * mm, "radius": 8 * mm});
            skCircle(sketch, "E2.45.11.0", {"center": v(1244.6, 127) * mm, "radius": 8 * mm});
            skCircle(sketch, "E2.45.12.0", {"center": v(1244.6, 177.8) * mm, "radius": 8 * mm});
            skCircle(sketch, "E2.45.13.0", {"center": v(1244.6, 228.6) * mm, "radius": 8 * mm});
            skCircle(sketch, "E2.45.14.0", {"center": v(1244.6, 279.4) * mm, "radius": 8 * mm});
            skCircle(sketch, "E2.45.15.0", {"center": v(1244.6, 330.2) * mm, "radius": 8 * mm});
            skCircle(sketch, "E2.45.16.0", {"center": v(1244.6, 381) * mm, "radius": 8 * mm});
            skCircle(sketch, "E2.45.17.0", {"center": v(1244.6, 431.8) * mm, "radius": 8 * mm});
            skCircle(sketch, "E2.46.0.0", {"center": v(1295.4, -431.8) * mm, "radius": 8 * mm});
            skCircle(sketch, "E2.46.1.0", {"center": v(1295.4, -381) * mm, "radius": 8 * mm});
            skCircle(sketch, "E2.46.2.0", {"center": v(1295.4, -330.2) * mm, "radius": 8 * mm});
            skCircle(sketch, "E2.46.3.0", {"center": v(1295.4, -279.4) * mm, "radius": 8 * mm});
            skCircle(sketch, "E2.46.4.0", {"center": v(1295.4, -228.6) * mm, "radius": 8 * mm});
            skCircle(sketch, "E2.46.5.0", {"center": v(1295.4, -177.8) * mm, "radius": 8 * mm});
            skCircle(sketch, "E2.46.6.0", {"center": v(1295.4, -127) * mm, "radius": 8 * mm});
            skCircle(sketch, "E2.46.7.0", {"center": v(1295.4, -76.2) * mm, "radius": 8 * mm});
            skCircle(sketch, "E2.46.8.0", {"center": v(1295.4, -25.4) * mm, "radius": 8 * mm});
            skCircle(sketch, "E2.46.9.0", {"center": v(1295.4, 25.4) * mm, "radius": 8 * mm});
            skCircle(sketch, "E2.46.10.0", {"center": v(1295.4, 76.2) * mm, "radius": 8 * mm});
            skCircle(sketch, "E2.46.11.0", {"center": v(1295.4, 127) * mm, "radius": 8 * mm});
            skCircle(sketch, "E2.46.12.0", {"center": v(1295.4, 177.8) * mm, "radius": 8 * mm});
            skCircle(sketch, "E2.46.13.0", {"center": v(1295.4, 228.6) * mm, "radius": 8 * mm});
            skCircle(sketch, "E2.46.14.0", {"center": v(1295.4, 279.4) * mm, "radius": 8 * mm});
            skCircle(sketch, "E2.46.15.0", {"center": v(1295.4, 330.2) * mm, "radius": 8 * mm});
            skCircle(sketch, "E2.46.16.0", {"center": v(1295.4, 381) * mm, "radius": 8 * mm});
            skCircle(sketch, "E2.46.17.0", {"center": v(1295.4, 431.8) * mm, "radius": 8 * mm});
            skCircle(sketch, "E2.47.0.0", {"center": v(1346.2, -431.8) * mm, "radius": 8 * mm});
            skCircle(sketch, "E2.47.1.0", {"center": v(1346.2, -381) * mm, "radius": 8 * mm});
            skCircle(sketch, "E2.47.2.0", {"center": v(1346.2, -330.2) * mm, "radius": 8 * mm});
            skCircle(sketch, "E2.47.3.0", {"center": v(1346.2, -279.4) * mm, "radius": 8 * mm});
            skCircle(sketch, "E2.47.4.0", {"center": v(1346.2, -228.6) * mm, "radius": 8 * mm});
            skCircle(sketch, "E2.47.5.0", {"center": v(1346.2, -177.8) * mm, "radius": 8 * mm});
            skCircle(sketch, "E2.47.6.0", {"center": v(1346.2, -127) * mm, "radius": 8 * mm});
            skCircle(sketch, "E2.47.7.0", {"center": v(1346.2, -76.2) * mm, "radius": 8 * mm});
            skCircle(sketch, "E2.47.8.0", {"center": v(1346.2, -25.4) * mm, "radius": 8 * mm});
            skCircle(sketch, "E2.47.9.0", {"center": v(1346.2, 25.4) * mm, "radius": 8 * mm});
            skCircle(sketch, "E2.47.10.0", {"center": v(1346.2, 76.2) * mm, "radius": 8 * mm});
            skCircle(sketch, "E2.47.11.0", {"center": v(1346.2, 127) * mm, "radius": 8 * mm});
            skCircle(sketch, "E2.47.12.0", {"center": v(1346.2, 177.8) * mm, "radius": 8 * mm});
            skCircle(sketch, "E2.47.13.0", {"center": v(1346.2, 228.6) * mm, "radius": 8 * mm});
            skCircle(sketch, "E2.47.14.0", {"center": v(1346.2, 279.4) * mm, "radius": 8 * mm});
            skCircle(sketch, "E2.47.15.0", {"center": v(1346.2, 330.2) * mm, "radius": 8 * mm});
            skCircle(sketch, "E2.47.16.0", {"center": v(1346.2, 381) * mm, "radius": 8 * mm});
            skCircle(sketch, "E2.47.17.0", {"center": v(1346.2, 431.8) * mm, "radius": 8 * mm});
            skLineSegment(sketch, "E2.direction1", {"start": v(-1041.4, -431.8) * mm, "end": v(-990.6, -431.8) * mm, "construction": true});
            skLineSegment(sketch, "E2.direction2", {"start": v(-1041.4, -431.8) * mm, "end": v(-1041.4, -381) * mm, "construction": true});
            skSolve(sketch);
        }
        {
            var Q0;
            Q0 = qSketchRegion(id + "F2", true);
            extrude(context, id + "F3", {"entities" : qUnion([Q0]), "operationType" : NewBodyOperationType.REMOVE, "endBound" : BoundingType.THROUGH_ALL, "oppositeDirection" : true, "depth" : 25.4 * mm});
        }
    });
